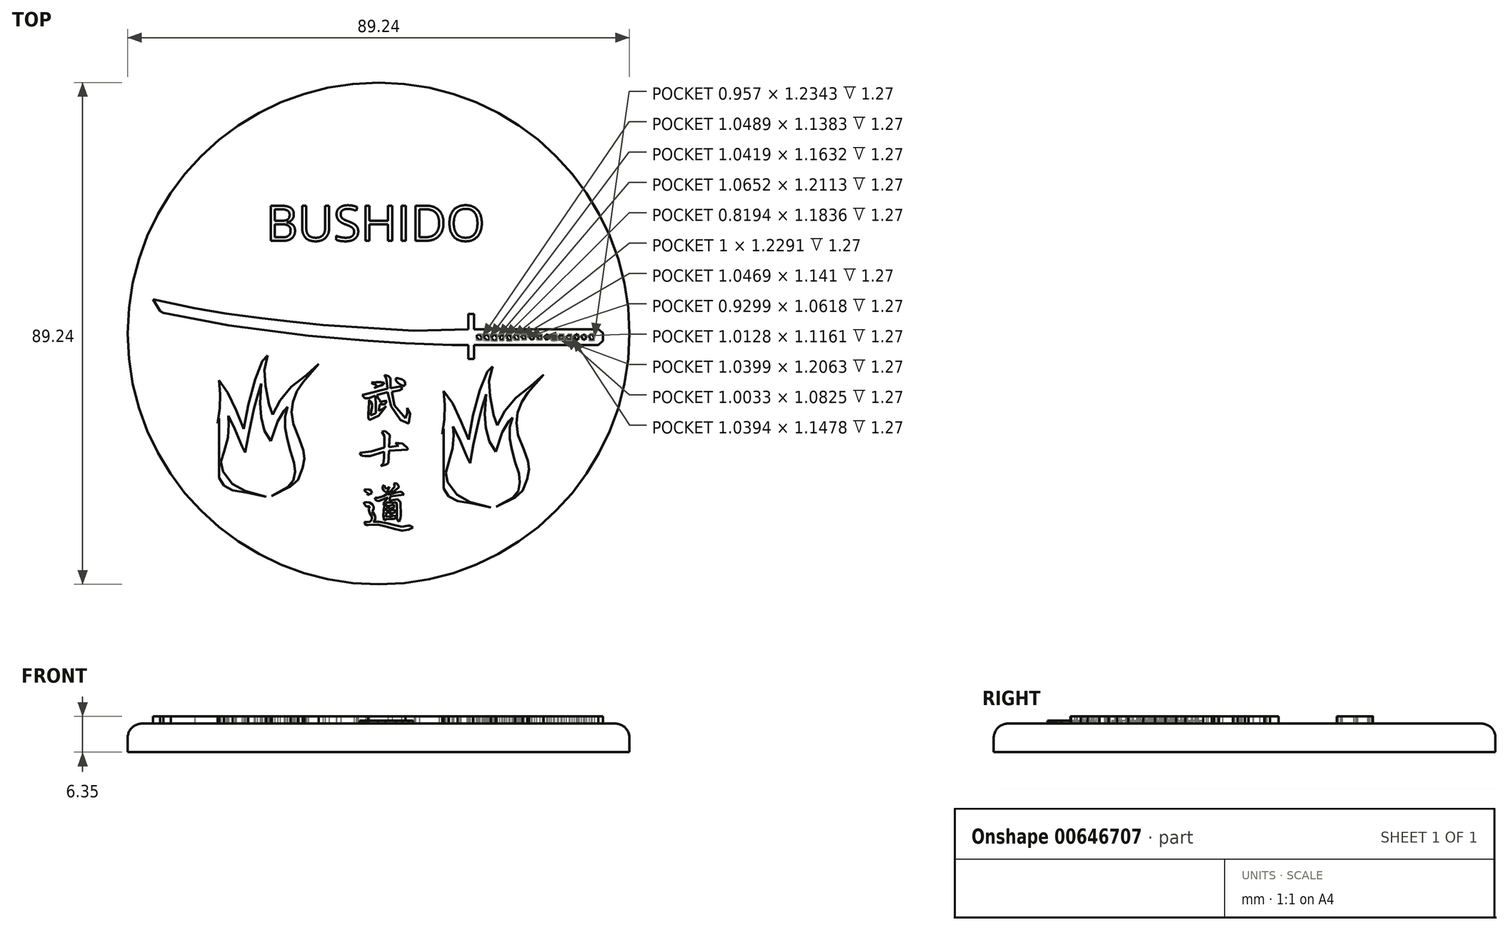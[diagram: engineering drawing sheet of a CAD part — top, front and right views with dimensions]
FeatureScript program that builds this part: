
annotation { "Feature Type Name" : "Feature", "Feature Type Description" : "" }
export const myFeature = defineFeature(function(context is Context, id is Id, definition is map)
    precondition{}
    {
        {
            var Q0;
            Q0=qCreatedBy(makeId("Top.planeOp"),FACE);
            var sketch = newSketch(context, id + "F0", { "sketchPlane" : qUnion([Q0])});
            skCircle(sketch, "E0", {"center": v(38.1, 0) * mm, "radius": 44.62 * mm});
            skSolve(sketch);
        }
        {
            var Q0;
            Q0 = qSketchRegion(id + "F0", true);
            extrude(context, id + "F1", {"entities" : qUnion([Q0]), "oppositeDirection" : true, "depth" : 5.08 * mm, "offsetDistance" : 25.4 * mm});
        }
        {
            var Q0;
            Q0=makeQuery(id+"F1.opExtrude","CAP_EDGE",EDGE,{"disambiguationData":[OSD([sQuery(id+"F0.wireOp",EDGE,"E0")])],"isStart":true});
            fillet(context, id + "F2", {"entities" : qUnion([Q0]), "radius" : 2.54 * mm, "tangentPropagation" : true, "allowEdgeOverflow" : false});
        }
        {
            var Q0;
            Q0=qCreatedBy(makeId("Top.planeOp"),FACE);
            var sketch = newSketch(context, id + "F3", { "sketchPlane" : qUnion([Q0])});
            skText(sketch, "E1", { "text": "BUSHIDO", "fontName": "OpenSans-Regular.ttf"});
            const initialGuessF3  = {"E1": [0.01806, 0.01647, 1, 0, 0.0063]};
            skSetInitialGuess(sketch, initialGuessF3);
            skSolve(sketch);
        }
        {
            var Q0;
            Q0 = qSketchRegion(id + "F3", true);
            extrude(context, id + "F4", {"entities" : qUnion([Q0]), "operationType" : NewBodyOperationType.ADD, "depth" : 1.27 * mm, "offsetDistance" : 25.4 * mm});
        }
        {
            var Q0;
            Q0=qCreatedBy(makeId("Top.planeOp"),FACE);
            var sketch = newSketch(context, id + "F5", { "sketchPlane" : qUnion([Q0])});
            skFitSpline(sketch, "E2", {"points": [v(36.87, -8.8) * mm, v(39.08, -8.86) * mm, v(37.37, -9.64) * mm, v(37.76, -9.3) * mm, v(36.87, -8.8) * mm]});
            skFitSpline(sketch, "E3", {"points": [v(41.13, -8.13) * mm, v(42.6, -9.31) * mm, v(42.62, -8.43) * mm, v(41.13, -8.13) * mm]});
            skLineSegment(sketch, "E4", {"start": v(39.12, -7.4) * mm, "end": v(39.8, -7.55) * mm});
            skLineSegment(sketch, "E5", {"start": v(39.8, -7.55) * mm, "end": v(40.25, -8) * mm});
            skLineSegment(sketch, "E6", {"start": v(40.25, -8) * mm, "end": v(40.25, -9.71) * mm});
            skLineSegment(sketch, "E7", {"start": v(40.25, -9.71) * mm, "end": v(41.91, -9.43) * mm});
            skLineSegment(sketch, "E8", {"start": v(41.91, -9.43) * mm, "end": v(42.4, -9.8) * mm});
            skLineSegment(sketch, "E9", {"start": v(42.4, -9.8) * mm, "end": v(41.8, -10.12) * mm});
            skLineSegment(sketch, "E10", {"start": v(41.8, -10.12) * mm, "end": v(40.46, -10.36) * mm});
            skLineSegment(sketch, "E11", {"start": v(40.46, -10.36) * mm, "end": v(40.91, -12.82) * mm});
            skLineSegment(sketch, "E12", {"start": v(40.91, -12.82) * mm, "end": v(42.89, -15.1) * mm});
            skLineSegment(sketch, "E13", {"start": v(42.89, -15.1) * mm, "end": v(43.22, -14.21) * mm});
            skLineSegment(sketch, "E14", {"start": v(43.22, -14.21) * mm, "end": v(43.22, -13.25) * mm});
            skLineSegment(sketch, "E15", {"start": v(43.22, -13.25) * mm, "end": v(43.7, -14.33) * mm});
            skLineSegment(sketch, "E16", {"start": v(43.7, -14.33) * mm, "end": v(43.48, -16.01) * mm});
            skLineSegment(sketch, "E17", {"start": v(43.48, -16.01) * mm, "end": v(42, -15.42) * mm});
            skLineSegment(sketch, "E18", {"start": v(42, -15.42) * mm, "end": v(40.34, -13) * mm});
            skLineSegment(sketch, "E19", {"start": v(40.34, -13) * mm, "end": v(39.71, -10.46) * mm});
            skLineSegment(sketch, "E20", {"start": v(39.71, -10.46) * mm, "end": v(37.83, -10.93) * mm});
            skLineSegment(sketch, "E21", {"start": v(37.83, -10.93) * mm, "end": v(37.97, -11.5) * mm});
            skLineSegment(sketch, "E22", {"start": v(37.97, -11.5) * mm, "end": v(38.35, -11.88) * mm});
            skLineSegment(sketch, "E23", {"start": v(38.35, -11.88) * mm, "end": v(38.35, -12.22) * mm});
            skLineSegment(sketch, "E24", {"start": v(38.35, -12.22) * mm, "end": v(39.04, -12.01) * mm});
            skLineSegment(sketch, "E25", {"start": v(39.04, -12.01) * mm, "end": v(39.58, -12.01) * mm});
            skLineSegment(sketch, "E26", {"start": v(39.58, -12.01) * mm, "end": v(39.22, -12.62) * mm});
            skLineSegment(sketch, "E27", {"start": v(39.22, -12.62) * mm, "end": v(38.32, -12.62) * mm});
            skLineSegment(sketch, "E28", {"start": v(38.32, -12.62) * mm, "end": v(38.1, -13.77) * mm});
            skLineSegment(sketch, "E29", {"start": v(38.1, -13.77) * mm, "end": v(38.89, -13.4) * mm});
            skLineSegment(sketch, "E30", {"start": v(38.89, -13.4) * mm, "end": v(39.48, -12.91) * mm});
            skLineSegment(sketch, "E31", {"start": v(39.48, -12.91) * mm, "end": v(38.1, -14.61) * mm});
            skLineSegment(sketch, "E32", {"start": v(38.1, -14.61) * mm, "end": v(36.46, -15.42) * mm});
            skLineSegment(sketch, "E33", {"start": v(36.46, -15.42) * mm, "end": v(36.25, -15) * mm});
            skLineSegment(sketch, "E34", {"start": v(36.25, -15) * mm, "end": v(36.25, -14.29) * mm});
            skLineSegment(sketch, "E35", {"start": v(36.25, -14.29) * mm, "end": v(36.42, -12.37) * mm});
            skLineSegment(sketch, "E36", {"start": v(36.42, -12.37) * mm, "end": v(36.42, -11.82) * mm});
            skLineSegment(sketch, "E37", {"start": v(36.42, -11.82) * mm, "end": v(36.82, -12.28) * mm});
            skLineSegment(sketch, "E38", {"start": v(36.82, -12.28) * mm, "end": v(36.96, -12.83) * mm});
            skLineSegment(sketch, "E39", {"start": v(36.96, -12.83) * mm, "end": v(36.65, -14.56) * mm});
            skLineSegment(sketch, "E40", {"start": v(36.65, -14.56) * mm, "end": v(37.65, -14.17) * mm});
            skLineSegment(sketch, "E41", {"start": v(37.65, -14.17) * mm, "end": v(37.65, -12.26) * mm});
            skLineSegment(sketch, "E42", {"start": v(37.65, -12.26) * mm, "end": v(37.47, -11.07) * mm});
            skLineSegment(sketch, "E43", {"start": v(37.47, -11.07) * mm, "end": v(36.42, -11.5) * mm});
            skLineSegment(sketch, "E44", {"start": v(36.42, -11.5) * mm, "end": v(35.66, -11.5) * mm});
            skLineSegment(sketch, "E45", {"start": v(35.66, -11.5) * mm, "end": v(35.18, -10.96) * mm});
            skLineSegment(sketch, "E46", {"start": v(35.18, -10.96) * mm, "end": v(35.94, -10.79) * mm});
            skLineSegment(sketch, "E47", {"start": v(35.94, -10.79) * mm, "end": v(39.7, -9.8) * mm});
            skLineSegment(sketch, "E48", {"start": v(39.7, -9.8) * mm, "end": v(39.48, -7.93) * mm});
            skLineSegment(sketch, "E49", {"start": v(39.48, -7.93) * mm, "end": v(39.12, -7.4) * mm});
            skLineSegment(sketch, "E50", {"start": v(38.67, -17.5) * mm, "end": v(39.12, -17.36) * mm});
            skLineSegment(sketch, "E51", {"start": v(39.12, -17.36) * mm, "end": v(39.48, -17.5) * mm});
            skLineSegment(sketch, "E52", {"start": v(39.48, -17.5) * mm, "end": v(40.1, -18.05) * mm});
            skLineSegment(sketch, "E53", {"start": v(40.1, -18.05) * mm, "end": v(39.95, -20.19) * mm});
            skLineSegment(sketch, "E54", {"start": v(39.95, -20.19) * mm, "end": v(41.68, -19.95) * mm});
            skLineSegment(sketch, "E55", {"start": v(41.68, -19.95) * mm, "end": v(41.48, -19.87) * mm});
            skLineSegment(sketch, "E56", {"start": v(41.48, -19.87) * mm, "end": v(41.13, -19.45) * mm});
            skLineSegment(sketch, "E57", {"start": v(41.13, -19.45) * mm, "end": v(42.35, -19.6) * mm});
            skLineSegment(sketch, "E58", {"start": v(42.35, -19.6) * mm, "end": v(43.27, -20.43) * mm});
            skLineSegment(sketch, "E59", {"start": v(43.27, -20.43) * mm, "end": v(43.27, -20.67) * mm});
            skLineSegment(sketch, "E60", {"start": v(43.27, -20.67) * mm, "end": v(39.97, -20.88) * mm});
            skLineSegment(sketch, "E61", {"start": v(39.97, -20.88) * mm, "end": v(39.8, -23.09) * mm});
            skLineSegment(sketch, "E62", {"start": v(39.8, -23.09) * mm, "end": v(39.4, -23.33) * mm});
            skLineSegment(sketch, "E63", {"start": v(39.4, -23.33) * mm, "end": v(38.52, -23.59) * mm});
            skLineSegment(sketch, "E64", {"start": v(38.52, -23.59) * mm, "end": v(38.97, -23.12) * mm});
            skLineSegment(sketch, "E65", {"start": v(38.97, -23.12) * mm, "end": v(39.1, -22.1) * mm});
            skLineSegment(sketch, "E66", {"start": v(39.1, -22.1) * mm, "end": v(39.1, -21.04) * mm});
            skLineSegment(sketch, "E67", {"start": v(39.1, -21.04) * mm, "end": v(36.57, -21.83) * mm});
            skLineSegment(sketch, "E68", {"start": v(36.57, -21.83) * mm, "end": v(35.67, -21.83) * mm});
            skLineSegment(sketch, "E69", {"start": v(35.67, -21.83) * mm, "end": v(35.05, -21.75) * mm});
            skLineSegment(sketch, "E70", {"start": v(35.05, -21.75) * mm, "end": v(34.79, -21.22) * mm});
            skLineSegment(sketch, "E71", {"start": v(34.79, -21.22) * mm, "end": v(36.77, -21.01) * mm});
            skLineSegment(sketch, "E72", {"start": v(36.77, -21.01) * mm, "end": v(39.12, -20.3) * mm});
            skLineSegment(sketch, "E73", {"start": v(39.12, -20.3) * mm, "end": v(39.12, -18.27) * mm});
            skLineSegment(sketch, "E74", {"start": v(39.12, -18.27) * mm, "end": v(38.67, -17.5) * mm});
            skLineSegment(sketch, "E75", {"start": v(36.68, -23.95) * mm, "end": v(39.03, -23.68) * mm});
            skLineSegment(sketch, "E76", {"start": v(39.03, -23.68) * mm, "end": v(40.38, -23.47) * mm});
            skLineSegment(sketch, "E77", {"start": v(40.38, -23.47) * mm, "end": v(40.97, -23.31) * mm});
            skLineSegment(sketch, "E78", {"start": v(40.97, -23.31) * mm, "end": v(41.37, -23.33) * mm});
            skLineSegment(sketch, "E79", {"start": v(41.37, -23.33) * mm, "end": v(41.87, -23.54) * mm});
            skLineSegment(sketch, "E80", {"start": v(41.87, -23.54) * mm, "end": v(42.09, -24.07) * mm});
            skLineSegment(sketch, "E81", {"start": v(42.09, -24.07) * mm, "end": v(41.49, -24.07) * mm});
            skLineSegment(sketch, "E82", {"start": v(41.49, -24.07) * mm, "end": v(40.58, -24.07) * mm});
            skLineSegment(sketch, "E83", {"start": v(40.58, -24.07) * mm, "end": v(39.63, -24.07) * mm});
            skLineSegment(sketch, "E84", {"start": v(39.63, -24.07) * mm, "end": v(38.25, -24.4) * mm});
            skLineSegment(sketch, "E85", {"start": v(38.25, -24.4) * mm, "end": v(37.39, -24.54) * mm});
            skLineSegment(sketch, "E86", {"start": v(37.39, -24.54) * mm, "end": v(37.06, -24.4) * mm});
            skLineSegment(sketch, "E87", {"start": v(37.06, -24.4) * mm, "end": v(36.67, -23.98) * mm});
            skLineSegment(sketch, "E88", {"start": v(35.58, -27.68) * mm, "end": v(36.47, -27.8) * mm});
            skLineSegment(sketch, "E89", {"start": v(36.47, -27.8) * mm, "end": v(36.8, -27.96) * mm});
            skLineSegment(sketch, "E90", {"start": v(36.8, -27.96) * mm, "end": v(36.91, -28.4) * mm});
            skLineSegment(sketch, "E91", {"start": v(36.91, -28.4) * mm, "end": v(36.14, -28.72) * mm});
            skLineSegment(sketch, "E92", {"start": v(36.14, -28.72) * mm, "end": v(36.11, -28.5) * mm});
            skLineSegment(sketch, "E93", {"start": v(36.11, -28.5) * mm, "end": v(36.3, -28.47) * mm});
            skLineSegment(sketch, "E94", {"start": v(36.3, -28.47) * mm, "end": v(35.68, -28.12) * mm});
            skLineSegment(sketch, "E95", {"start": v(35.68, -28.12) * mm, "end": v(35.58, -27.68) * mm});
            skLineSegment(sketch, "E96", {"start": v(39.12, -26.98) * mm, "end": v(39.18, -27.25) * mm});
            skLineSegment(sketch, "E97", {"start": v(39.18, -27.25) * mm, "end": v(39.48, -27.62) * mm});
            skLineSegment(sketch, "E98", {"start": v(39.48, -27.62) * mm, "end": v(40.02, -27.28) * mm});
            skLineSegment(sketch, "E99", {"start": v(40.02, -27.28) * mm, "end": v(39.59, -28.37) * mm});
            skLineSegment(sketch, "E100", {"start": v(39.59, -28.37) * mm, "end": v(39.03, -28) * mm});
            skLineSegment(sketch, "E101", {"start": v(39.03, -28) * mm, "end": v(38.8, -27.55) * mm});
            skLineSegment(sketch, "E102", {"start": v(38.8, -27.55) * mm, "end": v(38.8, -27.17) * mm});
            skLineSegment(sketch, "E103", {"start": v(38.8, -27.17) * mm, "end": v(39.12, -26.98) * mm});
            skLineSegment(sketch, "E104", {"start": v(40.91, -26.65) * mm, "end": v(41.37, -26.7) * mm});
            skLineSegment(sketch, "E105", {"start": v(41.37, -26.7) * mm, "end": v(41.65, -27.13) * mm});
            skLineSegment(sketch, "E106", {"start": v(41.65, -27.13) * mm, "end": v(41.7, -27.39) * mm});
            skLineSegment(sketch, "E107", {"start": v(41.7, -27.39) * mm, "end": v(40.66, -28.2) * mm});
            skLineSegment(sketch, "E108", {"start": v(40.66, -28.2) * mm, "end": v(39.79, -28.58) * mm});
            skLineSegment(sketch, "E109", {"start": v(39.79, -28.58) * mm, "end": v(40.16, -28.63) * mm});
            skLineSegment(sketch, "E110", {"start": v(40.16, -28.63) * mm, "end": v(41.23, -28.26) * mm});
            skLineSegment(sketch, "E111", {"start": v(41.23, -28.26) * mm, "end": v(42.02, -28.17) * mm});
            skLineSegment(sketch, "E112", {"start": v(42.02, -28.17) * mm, "end": v(42.31, -28.29) * mm});
            skLineSegment(sketch, "E113", {"start": v(42.31, -28.29) * mm, "end": v(42.66, -28.63) * mm});
            skLineSegment(sketch, "E114", {"start": v(42.66, -28.63) * mm, "end": v(40.16, -28.98) * mm});
            skLineSegment(sketch, "E115", {"start": v(40.16, -28.98) * mm, "end": v(40.1, -29.66) * mm});
            skLineSegment(sketch, "E116", {"start": v(40.1, -29.66) * mm, "end": v(40, -29.8) * mm});
            skLineSegment(sketch, "E117", {"start": v(40, -29.8) * mm, "end": v(40.71, -29.6) * mm});
            skLineSegment(sketch, "E118", {"start": v(40.71, -29.6) * mm, "end": v(41.52, -29.48) * mm});
            skLineSegment(sketch, "E119", {"start": v(41.52, -29.48) * mm, "end": v(41.97, -29.97) * mm});
            skLineSegment(sketch, "E120", {"start": v(41.97, -29.97) * mm, "end": v(42.05, -32.42) * mm});
            skLineSegment(sketch, "E121", {"start": v(42.05, -32.42) * mm, "end": v(42, -32.78) * mm});
            skLineSegment(sketch, "E122", {"start": v(42, -32.78) * mm, "end": v(41.72, -33.48) * mm});
            skLineSegment(sketch, "E123", {"start": v(41.72, -33.48) * mm, "end": v(41.37, -33.06) * mm});
            skLineSegment(sketch, "E124", {"start": v(41.37, -33.06) * mm, "end": v(41.37, -31) * mm});
            skLineSegment(sketch, "E125", {"start": v(41.37, -31) * mm, "end": v(41.37, -30.48) * mm});
            skLineSegment(sketch, "E126", {"start": v(41.37, -30.48) * mm, "end": v(41.2, -30.01) * mm});
            skLineSegment(sketch, "E127", {"start": v(41.2, -30.01) * mm, "end": v(40.72, -30.12) * mm});
            skLineSegment(sketch, "E128", {"start": v(40.72, -30.12) * mm, "end": v(40.07, -30.04) * mm});
            skLineSegment(sketch, "E129", {"start": v(40.07, -30.04) * mm, "end": v(39.65, -30.04) * mm});
            skLineSegment(sketch, "E130", {"start": v(39.65, -30.04) * mm, "end": v(39.38, -30.22) * mm});
            skLineSegment(sketch, "E131", {"start": v(39.38, -30.22) * mm, "end": v(39.48, -30.6) * mm});
            skLineSegment(sketch, "E132", {"start": v(39.48, -30.6) * mm, "end": v(39.52, -30.7) * mm});
            skLineSegment(sketch, "E133", {"start": v(39.52, -30.7) * mm, "end": v(40.08, -30.62) * mm});
            skLineSegment(sketch, "E134", {"start": v(40.08, -30.62) * mm, "end": v(40.54, -30.5) * mm});
            skLineSegment(sketch, "E135", {"start": v(40.54, -30.5) * mm, "end": v(40.82, -30.53) * mm});
            skLineSegment(sketch, "E136", {"start": v(40.82, -30.53) * mm, "end": v(41, -30.7) * mm});
            skLineSegment(sketch, "E137", {"start": v(41, -30.7) * mm, "end": v(40.77, -30.92) * mm});
            skLineSegment(sketch, "E138", {"start": v(40.77, -30.92) * mm, "end": v(40.23, -31.11) * mm});
            skLineSegment(sketch, "E139", {"start": v(40.23, -31.11) * mm, "end": v(39.96, -31.3) * mm});
            skLineSegment(sketch, "E140", {"start": v(39.96, -31.3) * mm, "end": v(39.89, -31.25) * mm});
            skLineSegment(sketch, "E141", {"start": v(39.89, -31.25) * mm, "end": v(40.08, -31.1) * mm});
            skLineSegment(sketch, "E142", {"start": v(40.08, -31.1) * mm, "end": v(39.97, -31.05) * mm});
            skLineSegment(sketch, "E143", {"start": v(39.97, -31.05) * mm, "end": v(39.45, -31.04) * mm});
            skLineSegment(sketch, "E144", {"start": v(39.45, -31.04) * mm, "end": v(39.45, -31.55) * mm});
            skLineSegment(sketch, "E145", {"start": v(39.45, -31.55) * mm, "end": v(39.88, -31.55) * mm});
            skLineSegment(sketch, "E146", {"start": v(39.88, -31.55) * mm, "end": v(40.56, -31.39) * mm});
            skLineSegment(sketch, "E147", {"start": v(40.56, -31.39) * mm, "end": v(40.92, -31.39) * mm});
            skLineSegment(sketch, "E148", {"start": v(40.92, -31.39) * mm, "end": v(41.1, -31.54) * mm});
            skLineSegment(sketch, "E149", {"start": v(41.1, -31.54) * mm, "end": v(41.01, -31.77) * mm});
            skLineSegment(sketch, "E150", {"start": v(41.01, -31.77) * mm, "end": v(40.5, -32) * mm});
            skLineSegment(sketch, "E151", {"start": v(40.5, -32) * mm, "end": v(40.14, -32.26) * mm});
            skLineSegment(sketch, "E152", {"start": v(40.14, -32.26) * mm, "end": v(40.1, -32.2) * mm});
            skLineSegment(sketch, "E153", {"start": v(40.1, -32.2) * mm, "end": v(40.4, -31.9) * mm});
            skLineSegment(sketch, "E154", {"start": v(40.4, -31.9) * mm, "end": v(39.5, -31.82) * mm});
            skLineSegment(sketch, "E155", {"start": v(39.5, -31.82) * mm, "end": v(39.43, -32) * mm});
            skLineSegment(sketch, "E156", {"start": v(39.43, -32) * mm, "end": v(39.4, -32.6) * mm});
            skLineSegment(sketch, "E157", {"start": v(39.4, -32.6) * mm, "end": v(39.68, -32.47) * mm});
            skLineSegment(sketch, "E158", {"start": v(39.68, -32.47) * mm, "end": v(39.66, -32.54) * mm});
            skLineSegment(sketch, "E159", {"start": v(39.66, -32.54) * mm, "end": v(40.06, -32.58) * mm});
            skLineSegment(sketch, "E160", {"start": v(40.06, -32.58) * mm, "end": v(40.73, -32.43) * mm});
            skLineSegment(sketch, "E161", {"start": v(40.73, -32.43) * mm, "end": v(41.09, -32.5) * mm});
            skLineSegment(sketch, "E162", {"start": v(41.09, -32.5) * mm, "end": v(41.24, -32.77) * mm});
            skLineSegment(sketch, "E163", {"start": v(41.24, -32.77) * mm, "end": v(41.2, -32.87) * mm});
            skLineSegment(sketch, "E164", {"start": v(41.2, -32.87) * mm, "end": v(40.82, -32.96) * mm});
            skLineSegment(sketch, "E165", {"start": v(40.82, -32.96) * mm, "end": v(40.08, -32.96) * mm});
            skLineSegment(sketch, "E166", {"start": v(40.08, -32.96) * mm, "end": v(39.52, -33.03) * mm});
            skLineSegment(sketch, "E167", {"start": v(39.52, -33.03) * mm, "end": v(39.17, -33.23) * mm});
            skLineSegment(sketch, "E168", {"start": v(39.17, -33.23) * mm, "end": v(38.92, -32.52) * mm});
            skLineSegment(sketch, "E169", {"start": v(38.92, -32.52) * mm, "end": v(39.01, -31.43) * mm});
            skLineSegment(sketch, "E170", {"start": v(39.01, -31.43) * mm, "end": v(39.1, -30.66) * mm});
            skLineSegment(sketch, "E171", {"start": v(39.1, -30.66) * mm, "end": v(38.97, -30.25) * mm});
            skLineSegment(sketch, "E172", {"start": v(38.97, -30.25) * mm, "end": v(39.77, -29.15) * mm});
            skLineSegment(sketch, "E173", {"start": v(39.77, -29.15) * mm, "end": v(38.12, -29.79) * mm});
            skLineSegment(sketch, "E174", {"start": v(38.12, -29.79) * mm, "end": v(37.73, -29.75) * mm});
            skLineSegment(sketch, "E175", {"start": v(37.73, -29.75) * mm, "end": v(37.5, -29.5) * mm});
            skLineSegment(sketch, "E176", {"start": v(37.5, -29.5) * mm, "end": v(37.46, -29.23) * mm});
            skLineSegment(sketch, "E177", {"start": v(37.46, -29.23) * mm, "end": v(38.03, -29.23) * mm});
            skLineSegment(sketch, "E178", {"start": v(38.03, -29.23) * mm, "end": v(39.04, -28.91) * mm});
            skLineSegment(sketch, "E179", {"start": v(39.04, -28.91) * mm, "end": v(40.1, -28.19) * mm});
            skLineSegment(sketch, "E180", {"start": v(40.1, -28.19) * mm, "end": v(40.98, -27.24) * mm});
            skLineSegment(sketch, "E181", {"start": v(40.98, -27.24) * mm, "end": v(40.9, -26.92) * mm});
            skLineSegment(sketch, "E182", {"start": v(40.9, -26.92) * mm, "end": v(40.85, -26.71) * mm});
            skLineSegment(sketch, "E183", {"start": v(40.85, -26.71) * mm, "end": v(40.92, -26.63) * mm});
            skLineSegment(sketch, "E184", {"start": v(40.92, -26.63) * mm, "end": v(40.91, -26.65) * mm});
            skLineSegment(sketch, "E185", {"start": v(35.52, -30.07) * mm, "end": v(35.98, -30.02) * mm});
            skLineSegment(sketch, "E186", {"start": v(35.98, -30.02) * mm, "end": v(36.47, -30.08) * mm});
            skLineSegment(sketch, "E187", {"start": v(36.47, -30.08) * mm, "end": v(37, -30.38) * mm});
            skLineSegment(sketch, "E188", {"start": v(37, -30.38) * mm, "end": v(37.22, -30.76) * mm});
            skLineSegment(sketch, "E189", {"start": v(37.22, -30.76) * mm, "end": v(37.22, -31.2) * mm});
            skLineSegment(sketch, "E190", {"start": v(37.22, -31.2) * mm, "end": v(36.95, -31.62) * mm});
            skLineSegment(sketch, "E191", {"start": v(36.95, -31.62) * mm, "end": v(37.42, -32.38) * mm});
            skLineSegment(sketch, "E192", {"start": v(37.42, -32.38) * mm, "end": v(37.53, -32.82) * mm});
            skLineSegment(sketch, "E193", {"start": v(37.53, -32.82) * mm, "end": v(37.43, -33.26) * mm});
            skLineSegment(sketch, "E194", {"start": v(37.43, -33.26) * mm, "end": v(37.14, -33.5) * mm});
            skLineSegment(sketch, "E195", {"start": v(37.14, -33.5) * mm, "end": v(38.1, -33.5) * mm});
            skLineSegment(sketch, "E196", {"start": v(38.1, -33.5) * mm, "end": v(39.56, -33.74) * mm});
            skLineSegment(sketch, "E197", {"start": v(39.56, -33.74) * mm, "end": v(41.1, -34.14) * mm});
            skLineSegment(sketch, "E198", {"start": v(41.1, -34.14) * mm, "end": v(42.26, -34.37) * mm});
            skLineSegment(sketch, "E199", {"start": v(42.26, -34.37) * mm, "end": v(43.32, -34.19) * mm});
            skLineSegment(sketch, "E200", {"start": v(43.32, -34.19) * mm, "end": v(43.79, -34.19) * mm});
            skLineSegment(sketch, "E201", {"start": v(43.79, -34.19) * mm, "end": v(44.23, -34.52) * mm});
            skLineSegment(sketch, "E202", {"start": v(44.23, -34.52) * mm, "end": v(43.48, -34.92) * mm});
            skLineSegment(sketch, "E203", {"start": v(43.48, -34.92) * mm, "end": v(42.28, -35.06) * mm});
            skLineSegment(sketch, "E204", {"start": v(42.28, -35.06) * mm, "end": v(41.16, -34.8) * mm});
            skLineSegment(sketch, "E205", {"start": v(41.16, -34.8) * mm, "end": v(39.3, -34.3) * mm});
            skLineSegment(sketch, "E206", {"start": v(39.3, -34.3) * mm, "end": v(37.97, -34.02) * mm});
            skLineSegment(sketch, "E207", {"start": v(37.97, -34.02) * mm, "end": v(36.27, -34.06) * mm});
            skLineSegment(sketch, "E208", {"start": v(36.27, -34.06) * mm, "end": v(35.94, -34.06) * mm});
            skLineSegment(sketch, "E209", {"start": v(35.94, -34.06) * mm, "end": v(35.64, -33.85) * mm});
            skLineSegment(sketch, "E210", {"start": v(35.64, -33.85) * mm, "end": v(35.64, -33.5) * mm});
            skLineSegment(sketch, "E211", {"start": v(35.64, -33.5) * mm, "end": v(36.1, -33.55) * mm});
            skLineSegment(sketch, "E212", {"start": v(36.1, -33.55) * mm, "end": v(36.6, -33.46) * mm});
            skLineSegment(sketch, "E213", {"start": v(36.6, -33.46) * mm, "end": v(36.95, -33.01) * mm});
            skLineSegment(sketch, "E214", {"start": v(36.95, -33.01) * mm, "end": v(36.95, -32.53) * mm});
            skLineSegment(sketch, "E215", {"start": v(36.95, -32.53) * mm, "end": v(36.46, -31.83) * mm});
            skLineSegment(sketch, "E216", {"start": v(36.46, -31.83) * mm, "end": v(36.35, -31.22) * mm});
            skLineSegment(sketch, "E217", {"start": v(36.35, -31.22) * mm, "end": v(36.54, -30.77) * mm});
            skLineSegment(sketch, "E218", {"start": v(36.54, -30.77) * mm, "end": v(36.3, -30.74) * mm});
            skLineSegment(sketch, "E219", {"start": v(36.3, -30.74) * mm, "end": v(35.93, -30.74) * mm});
            skLineSegment(sketch, "E220", {"start": v(35.93, -30.74) * mm, "end": v(35.63, -30.47) * mm});
            skLineSegment(sketch, "E221", {"start": v(35.63, -30.47) * mm, "end": v(35.52, -30.2) * mm});
            skLineSegment(sketch, "E222", {"start": v(35.52, -30.2) * mm, "end": v(35.52, -30.07) * mm});
            skSolve(sketch);
        }
        {
            var Q0;
            Q0 = qSketchRegion(id + "F5", true);
            extrude(context, id + "F6", {"entities" : qUnion([Q0]), "operationType" : NewBodyOperationType.ADD, "depth" : 0.5 * mm, "offsetDistance" : 25.4 * mm});
        }
        {
            var Q0;
            Q0=qCreatedBy(makeId("Top.planeOp"),FACE);
            var sketch = newSketch(context, id + "F7", { "sketchPlane" : qUnion([Q0])});
            skLineSegment(sketch, "E223", {"start": v(-64.44, 4.36) * mm, "end": v(-42.37, 4.36) * mm});
            skLineSegment(sketch, "E224", {"start": v(-42.37, 4.36) * mm, "end": v(-41.55, 3.73) * mm});
            skLineSegment(sketch, "E225", {"start": v(-41.55, 3.73) * mm, "end": v(-41.55, 2.36) * mm});
            skLineSegment(sketch, "E226", {"start": v(-41.55, 2.36) * mm, "end": v(-42.37, 1.59) * mm});
            skLineSegment(sketch, "E227", {"start": v(-42.37, 1.59) * mm, "end": v(-64.44, 1.59) * mm});
            skLineSegment(sketch, "E228", {"start": v(-65.5, 7.14) * mm, "end": v(-64.44, 7.14) * mm});
            skLineSegment(sketch, "E229", {"start": v(-64.44, 7.14) * mm, "end": v(-64.44, -0.92) * mm});
            skLineSegment(sketch, "E230", {"start": v(-64.44, -0.92) * mm, "end": v(-65.5, -0.88) * mm});
            skLineSegment(sketch, "E231", {"start": v(-65.5, -0.88) * mm, "end": v(-65.5, 7.14) * mm});
            skLineSegment(sketch, "E232", {"start": v(-63.55, 3.52) * mm, "end": v(-64.08, 3.1) * mm});
            skLineSegment(sketch, "E233", {"start": v(-64.08, 3.1) * mm, "end": v(-63.5, 2.39) * mm});
            skLineSegment(sketch, "E234", {"start": v(-63.5, 2.39) * mm, "end": v(-63.03, 2.77) * mm});
            skLineSegment(sketch, "E235", {"start": v(-63.03, 2.77) * mm, "end": v(-63.55, 3.52) * mm});
            skLineSegment(sketch, "E236", {"start": v(-62.23, 3.52) * mm, "end": v(-62.73, 2.95) * mm});
            skLineSegment(sketch, "E237", {"start": v(-62.73, 2.95) * mm, "end": v(-62.06, 2.36) * mm});
            skLineSegment(sketch, "E238", {"start": v(-62.06, 2.36) * mm, "end": v(-61.7, 2.78) * mm});
            skLineSegment(sketch, "E239", {"start": v(-61.7, 2.78) * mm, "end": v(-62.23, 3.52) * mm});
            skLineSegment(sketch, "E240", {"start": v(-60.84, 3.52) * mm, "end": v(-61.39, 2.82) * mm});
            skLineSegment(sketch, "E241", {"start": v(-61.39, 2.82) * mm, "end": v(-60.74, 2.31) * mm});
            skLineSegment(sketch, "E242", {"start": v(-60.74, 2.31) * mm, "end": v(-60.32, 2.84) * mm});
            skLineSegment(sketch, "E243", {"start": v(-60.32, 2.84) * mm, "end": v(-60.84, 3.52) * mm});
            skLineSegment(sketch, "E244", {"start": v(-59.55, 3.52) * mm, "end": v(-59.98, 2.9) * mm});
            skLineSegment(sketch, "E245", {"start": v(-59.98, 2.9) * mm, "end": v(-59.6, 2.34) * mm});
            skLineSegment(sketch, "E246", {"start": v(-59.6, 2.34) * mm, "end": v(-59.16, 2.89) * mm});
            skLineSegment(sketch, "E247", {"start": v(-59.16, 2.89) * mm, "end": v(-59.55, 3.52) * mm});
            skLineSegment(sketch, "E248", {"start": v(-58.23, 3.52) * mm, "end": v(-58.7, 3) * mm});
            skLineSegment(sketch, "E249", {"start": v(-58.7, 3) * mm, "end": v(-58.25, 2.3) * mm});
            skLineSegment(sketch, "E250", {"start": v(-58.25, 2.3) * mm, "end": v(-57.7, 2.65) * mm});
            skLineSegment(sketch, "E251", {"start": v(-57.7, 2.65) * mm, "end": v(-58.23, 3.52) * mm});
            skLineSegment(sketch, "E252", {"start": v(-56.9, 3.52) * mm, "end": v(-57.43, 3.02) * mm});
            skLineSegment(sketch, "E253", {"start": v(-57.43, 3.02) * mm, "end": v(-56.82, 2.38) * mm});
            skLineSegment(sketch, "E254", {"start": v(-56.82, 2.38) * mm, "end": v(-56.38, 2.77) * mm});
            skLineSegment(sketch, "E255", {"start": v(-56.38, 2.77) * mm, "end": v(-56.9, 3.52) * mm});
            skLineSegment(sketch, "E256", {"start": v(-55.59, 3.52) * mm, "end": v(-56.09, 3.1) * mm});
            skLineSegment(sketch, "E257", {"start": v(-56.09, 3.1) * mm, "end": v(-55.54, 2.46) * mm});
            skLineSegment(sketch, "E258", {"start": v(-55.54, 2.46) * mm, "end": v(-55.16, 2.8) * mm});
            skLineSegment(sketch, "E259", {"start": v(-55.16, 2.8) * mm, "end": v(-55.59, 3.52) * mm});
            skLineSegment(sketch, "E260", {"start": v(-54.17, 3.52) * mm, "end": v(-54.7, 3) * mm});
            skLineSegment(sketch, "E261", {"start": v(-54.7, 3) * mm, "end": v(-54.16, 2.47) * mm});
            skLineSegment(sketch, "E262", {"start": v(-54.16, 2.47) * mm, "end": v(-53.76, 2.8) * mm});
            skLineSegment(sketch, "E263", {"start": v(-53.76, 2.8) * mm, "end": v(-54.17, 3.52) * mm});
            skLineSegment(sketch, "E264", {"start": v(-52.79, 3.57) * mm, "end": v(-53.33, 3.1) * mm});
            skLineSegment(sketch, "E265", {"start": v(-53.33, 3.1) * mm, "end": v(-52.77, 2.45) * mm});
            skLineSegment(sketch, "E266", {"start": v(-52.77, 2.45) * mm, "end": v(-52.32, 2.85) * mm});
            skLineSegment(sketch, "E267", {"start": v(-52.32, 2.85) * mm, "end": v(-52.79, 3.57) * mm});
            skLineSegment(sketch, "E268", {"start": v(-51.37, 3.52) * mm, "end": v(-51.99, 3.07) * mm});
            skLineSegment(sketch, "E269", {"start": v(-51.99, 3.07) * mm, "end": v(-51.56, 2.5) * mm});
            skLineSegment(sketch, "E270", {"start": v(-51.56, 2.5) * mm, "end": v(-51.07, 2.86) * mm});
            skLineSegment(sketch, "E271", {"start": v(-51.07, 2.86) * mm, "end": v(-51.37, 3.52) * mm});
            skLineSegment(sketch, "E272", {"start": v(-50.15, 3.52) * mm, "end": v(-50.74, 3) * mm});
            skLineSegment(sketch, "E273", {"start": v(-50.74, 3) * mm, "end": v(-50.37, 2.32) * mm});
            skLineSegment(sketch, "E274", {"start": v(-50.37, 2.32) * mm, "end": v(-49.7, 2.68) * mm});
            skLineSegment(sketch, "E275", {"start": v(-49.7, 2.68) * mm, "end": v(-50.15, 3.52) * mm});
            skLineSegment(sketch, "E276", {"start": v(-48.85, 3.52) * mm, "end": v(-49.49, 3.05) * mm});
            skLineSegment(sketch, "E277", {"start": v(-49.49, 3.05) * mm, "end": v(-49.03, 2.44) * mm});
            skLineSegment(sketch, "E278", {"start": v(-49.03, 2.44) * mm, "end": v(-48.48, 2.85) * mm});
            skLineSegment(sketch, "E279", {"start": v(-48.48, 2.85) * mm, "end": v(-48.85, 3.52) * mm});
            skLineSegment(sketch, "E280", {"start": v(-47.46, 3.52) * mm, "end": v(-48.07, 3) * mm});
            skLineSegment(sketch, "E281", {"start": v(-48.07, 3) * mm, "end": v(-47.54, 2.38) * mm});
            skLineSegment(sketch, "E282", {"start": v(-47.54, 2.38) * mm, "end": v(-47.04, 2.8) * mm});
            skLineSegment(sketch, "E283", {"start": v(-47.04, 2.8) * mm, "end": v(-47.46, 3.52) * mm});
            skLineSegment(sketch, "E284", {"start": v(-46.07, 3.52) * mm, "end": v(-46.7, 3.16) * mm});
            skLineSegment(sketch, "E285", {"start": v(-46.7, 3.16) * mm, "end": v(-46.32, 2.48) * mm});
            skLineSegment(sketch, "E286", {"start": v(-46.32, 2.48) * mm, "end": v(-45.78, 2.78) * mm});
            skLineSegment(sketch, "E287", {"start": v(-45.78, 2.78) * mm, "end": v(-46.07, 3.52) * mm});
            skLineSegment(sketch, "E288", {"start": v(-44.8, 3.51) * mm, "end": v(-45.43, 3.16) * mm});
            skLineSegment(sketch, "E289", {"start": v(-45.43, 3.16) * mm, "end": v(-45.05, 2.46) * mm});
            skLineSegment(sketch, "E290", {"start": v(-45.05, 2.46) * mm, "end": v(-44.47, 2.78) * mm});
            skLineSegment(sketch, "E291", {"start": v(-44.47, 2.78) * mm, "end": v(-44.8, 3.51) * mm});
            skPoint(sketch, "E292.orphan", {"position": v(-44.77, 3.52) * mm});
            skLineSegment(sketch, "E293", {"start": v(-43.5, 3.59) * mm, "end": v(-44.02, 3.15) * mm});
            skPoint(sketch, "E293.endSnap0", {"position": v(-45.93, 3.15) * mm});
            skLineSegment(sketch, "E294", {"start": v(-44.02, 3.15) * mm, "end": v(-43.67, 2.36) * mm});
            skLineSegment(sketch, "E295", {"start": v(-43.67, 2.36) * mm, "end": v(-43.06, 2.86) * mm});
            skLineSegment(sketch, "E296", {"start": v(-43.06, 2.86) * mm, "end": v(-43.5, 3.59) * mm});
            skLineSegment(sketch, "E297", {"start": v(-65.5, 4.36) * mm, "end": v(-67.4, 3.28) * mm});
            skLineSegment(sketch, "E298", {"start": v(-67.4, 3.28) * mm, "end": v(-65.5, 1.59) * mm});
            skLineSegment(sketch, "E299", {"start": v(-65.5, 1.59) * mm, "end": v(-68.42, 1.59) * mm});
            skLineSegment(sketch, "E300", {"start": v(-68.42, 1.59) * mm, "end": v(-76.68, 1.9) * mm});
            skLineSegment(sketch, "E301", {"start": v(-76.68, 1.9) * mm, "end": v(-83.34, 2.32) * mm});
            skLineSegment(sketch, "E302", {"start": v(-83.34, 2.32) * mm, "end": v(-93.93, 3.22) * mm});
            skLineSegment(sketch, "E303", {"start": v(-93.93, 3.22) * mm, "end": v(-108.07, 5.1) * mm});
            skLineSegment(sketch, "E304", {"start": v(-108.07, 5.1) * mm, "end": v(-118.37, 7.03) * mm});
            skLineSegment(sketch, "E305", {"start": v(-118.37, 7.03) * mm, "end": v(-119.69, 7.31) * mm});
            skLineSegment(sketch, "E306", {"start": v(-119.69, 7.31) * mm, "end": v(-120.26, 7.6) * mm});
            skLineSegment(sketch, "E307", {"start": v(-120.26, 7.6) * mm, "end": v(-121.58, 9.69) * mm});
            skLineSegment(sketch, "E308", {"start": v(-121.58, 9.69) * mm, "end": v(-114.1, 8.15) * mm});
            skLineSegment(sketch, "E309", {"start": v(-114.1, 8.15) * mm, "end": v(-108.53, 7.2) * mm});
            skLineSegment(sketch, "E310", {"start": v(-108.53, 7.2) * mm, "end": v(-102.21, 6.32) * mm});
            skLineSegment(sketch, "E311", {"start": v(-102.21, 6.32) * mm, "end": v(-97.2, 5.78) * mm});
            skLineSegment(sketch, "E312", {"start": v(-97.2, 5.78) * mm, "end": v(-91.32, 5.17) * mm});
            skLineSegment(sketch, "E313", {"start": v(-91.32, 5.17) * mm, "end": v(-86.25, 4.85) * mm});
            skLineSegment(sketch, "E314", {"start": v(-86.25, 4.85) * mm, "end": v(-80.05, 4.46) * mm});
            skLineSegment(sketch, "E315", {"start": v(-80.05, 4.46) * mm, "end": v(-75.13, 4.15) * mm});
            skLineSegment(sketch, "E316", {"start": v(-75.13, 4.15) * mm, "end": v(-65.5, 4.36) * mm});
            skLineSegment(sketch, "E317", {"start": v(-67.4, 3.28) * mm, "end": v(-74.3, 3.59) * mm});
            skLineSegment(sketch, "E318", {"start": v(-74.3, 3.59) * mm, "end": v(-82.93, 3.96) * mm});
            skLineSegment(sketch, "E319", {"start": v(-82.93, 3.96) * mm, "end": v(-86.54, 4.19) * mm});
            skLineSegment(sketch, "E320", {"start": v(-86.54, 4.19) * mm, "end": v(-90.92, 4.46) * mm});
            skLineSegment(sketch, "E321", {"start": v(-90.92, 4.46) * mm, "end": v(-94.51, 4.85) * mm});
            skLineSegment(sketch, "E322", {"start": v(-94.51, 4.85) * mm, "end": v(-98.3, 5.26) * mm});
            skLineSegment(sketch, "E323", {"start": v(-98.3, 5.26) * mm, "end": v(-104.8, 5.99) * mm});
            skLineSegment(sketch, "E324", {"start": v(-104.8, 5.99) * mm, "end": v(-109.5, 6.64) * mm});
            skLineSegment(sketch, "E325", {"start": v(-109.5, 6.64) * mm, "end": v(-115.26, 7.67) * mm});
            skLineSegment(sketch, "E326", {"start": v(-115.26, 7.67) * mm, "end": v(-119.16, 8.53) * mm});
            skLineSegment(sketch, "E327", {"start": v(-119.16, 8.53) * mm, "end": v(-121.58, 9.69) * mm});
            skLineSegment(sketch, "E328", {"start": v(55.1, 0.72) * mm, "end": v(77.18, 0.72) * mm});
            skLineSegment(sketch, "E329", {"start": v(77.18, 0.72) * mm, "end": v(78, 0.09) * mm});
            skLineSegment(sketch, "E330", {"start": v(78, 0.09) * mm, "end": v(78, -1.28) * mm});
            skLineSegment(sketch, "E331", {"start": v(78, -1.28) * mm, "end": v(77.18, -2.05) * mm});
            skLineSegment(sketch, "E332", {"start": v(77.18, -2.05) * mm, "end": v(55.1, -2.05) * mm});
            skLineSegment(sketch, "E333", {"start": v(54.05, 3.5) * mm, "end": v(55.1, 3.5) * mm});
            skLineSegment(sketch, "E334", {"start": v(55.1, 3.5) * mm, "end": v(55.1, -4.56) * mm});
            skLineSegment(sketch, "E335", {"start": v(55.1, -4.56) * mm, "end": v(54.05, -4.52) * mm});
            skLineSegment(sketch, "E336", {"start": v(54.05, -4.52) * mm, "end": v(54.05, 3.5) * mm});
            skLineSegment(sketch, "E337", {"start": v(56, -0.12) * mm, "end": v(55.47, -0.55) * mm});
            skLineSegment(sketch, "E338", {"start": v(55.47, -0.55) * mm, "end": v(56.05, -1.26) * mm});
            skLineSegment(sketch, "E339", {"start": v(56.05, -1.26) * mm, "end": v(56.52, -0.87) * mm});
            skLineSegment(sketch, "E340", {"start": v(56.52, -0.87) * mm, "end": v(56, -0.12) * mm});
            skLineSegment(sketch, "E341", {"start": v(57.31, -0.12) * mm, "end": v(56.81, -0.69) * mm});
            skLineSegment(sketch, "E342", {"start": v(56.81, -0.69) * mm, "end": v(57.49, -1.28) * mm});
            skLineSegment(sketch, "E343", {"start": v(57.49, -1.28) * mm, "end": v(57.85, -0.86) * mm});
            skLineSegment(sketch, "E344", {"start": v(57.85, -0.86) * mm, "end": v(57.31, -0.12) * mm});
            skLineSegment(sketch, "E345", {"start": v(58.7, -0.12) * mm, "end": v(58.15, -0.82) * mm});
            skLineSegment(sketch, "E346", {"start": v(58.15, -0.82) * mm, "end": v(58.8, -1.33) * mm});
            skLineSegment(sketch, "E347", {"start": v(58.8, -1.33) * mm, "end": v(59.22, -0.8) * mm});
            skLineSegment(sketch, "E348", {"start": v(59.22, -0.8) * mm, "end": v(58.7, -0.12) * mm});
            skLineSegment(sketch, "E349", {"start": v(60, -0.12) * mm, "end": v(59.56, -0.73) * mm});
            skLineSegment(sketch, "E350", {"start": v(59.56, -0.73) * mm, "end": v(59.95, -1.3) * mm});
            skLineSegment(sketch, "E351", {"start": v(59.95, -1.3) * mm, "end": v(60.38, -0.75) * mm});
            skLineSegment(sketch, "E352", {"start": v(60.38, -0.75) * mm, "end": v(60, -0.12) * mm});
            skLineSegment(sketch, "E353", {"start": v(61.32, -0.12) * mm, "end": v(60.84, -0.64) * mm});
            skLineSegment(sketch, "E354", {"start": v(60.84, -0.64) * mm, "end": v(61.3, -1.35) * mm});
            skLineSegment(sketch, "E355", {"start": v(61.3, -1.35) * mm, "end": v(61.84, -1) * mm});
            skLineSegment(sketch, "E356", {"start": v(61.84, -1) * mm, "end": v(61.32, -0.12) * mm});
            skLineSegment(sketch, "E357", {"start": v(62.64, -0.12) * mm, "end": v(62.11, -0.62) * mm});
            skLineSegment(sketch, "E358", {"start": v(62.11, -0.62) * mm, "end": v(62.73, -1.26) * mm});
            skLineSegment(sketch, "E359", {"start": v(62.73, -1.26) * mm, "end": v(63.16, -0.87) * mm});
            skLineSegment(sketch, "E360", {"start": v(63.16, -0.87) * mm, "end": v(62.64, -0.12) * mm});
            skLineSegment(sketch, "E361", {"start": v(63.96, -0.12) * mm, "end": v(63.46, -0.55) * mm});
            skLineSegment(sketch, "E362", {"start": v(63.46, -0.55) * mm, "end": v(64, -1.18) * mm});
            skLineSegment(sketch, "E363", {"start": v(64, -1.18) * mm, "end": v(64.39, -0.85) * mm});
            skLineSegment(sketch, "E364", {"start": v(64.39, -0.85) * mm, "end": v(63.96, -0.12) * mm});
            skLineSegment(sketch, "E365", {"start": v(65.37, -0.12) * mm, "end": v(64.85, -0.64) * mm});
            skLineSegment(sketch, "E366", {"start": v(64.85, -0.64) * mm, "end": v(65.38, -1.18) * mm});
            skLineSegment(sketch, "E367", {"start": v(65.38, -1.18) * mm, "end": v(65.78, -0.85) * mm});
            skLineSegment(sketch, "E368", {"start": v(65.78, -0.85) * mm, "end": v(65.37, -0.12) * mm});
            skLineSegment(sketch, "E369", {"start": v(66.76, -0.07) * mm, "end": v(66.21, -0.55) * mm});
            skLineSegment(sketch, "E370", {"start": v(66.21, -0.55) * mm, "end": v(66.77, -1.19) * mm});
            skLineSegment(sketch, "E371", {"start": v(66.77, -1.19) * mm, "end": v(67.22, -0.8) * mm});
            skLineSegment(sketch, "E372", {"start": v(67.22, -0.8) * mm, "end": v(66.76, -0.07) * mm});
            skLineSegment(sketch, "E373", {"start": v(68.17, -0.12) * mm, "end": v(67.55, -0.57) * mm});
            skLineSegment(sketch, "E374", {"start": v(67.55, -0.57) * mm, "end": v(67.98, -1.15) * mm});
            skLineSegment(sketch, "E375", {"start": v(67.98, -1.15) * mm, "end": v(68.47, -0.78) * mm});
            skLineSegment(sketch, "E376", {"start": v(68.47, -0.78) * mm, "end": v(68.17, -0.12) * mm});
            skLineSegment(sketch, "E377", {"start": v(69.4, -0.12) * mm, "end": v(68.8, -0.64) * mm});
            skLineSegment(sketch, "E378", {"start": v(68.8, -0.64) * mm, "end": v(69.17, -1.32) * mm});
            skLineSegment(sketch, "E379", {"start": v(69.17, -1.32) * mm, "end": v(69.85, -0.96) * mm});
            skLineSegment(sketch, "E380", {"start": v(69.85, -0.96) * mm, "end": v(69.4, -0.12) * mm});
            skLineSegment(sketch, "E381", {"start": v(70.7, -0.12) * mm, "end": v(70.06, -0.6) * mm});
            skLineSegment(sketch, "E382", {"start": v(70.06, -0.6) * mm, "end": v(70.51, -1.2) * mm});
            skLineSegment(sketch, "E383", {"start": v(70.51, -1.2) * mm, "end": v(71.06, -0.79) * mm});
            skLineSegment(sketch, "E384", {"start": v(71.06, -0.79) * mm, "end": v(70.7, -0.12) * mm});
            skLineSegment(sketch, "E385", {"start": v(72.08, -0.12) * mm, "end": v(71.47, -0.64) * mm});
            skLineSegment(sketch, "E386", {"start": v(71.47, -0.64) * mm, "end": v(72, -1.26) * mm});
            skLineSegment(sketch, "E387", {"start": v(72, -1.26) * mm, "end": v(72.5, -0.83) * mm});
            skLineSegment(sketch, "E388", {"start": v(72.5, -0.83) * mm, "end": v(72.08, -0.12) * mm});
            skLineSegment(sketch, "E389", {"start": v(73.47, -0.12) * mm, "end": v(72.83, -0.48) * mm});
            skLineSegment(sketch, "E390", {"start": v(72.83, -0.48) * mm, "end": v(73.22, -1.17) * mm});
            skLineSegment(sketch, "E391", {"start": v(73.22, -1.17) * mm, "end": v(73.76, -0.86) * mm});
            skLineSegment(sketch, "E392", {"start": v(73.76, -0.86) * mm, "end": v(73.47, -0.12) * mm});
            skLineSegment(sketch, "E393", {"start": v(74.75, -0.13) * mm, "end": v(74.1, -0.48) * mm});
            skLineSegment(sketch, "E394", {"start": v(74.1, -0.48) * mm, "end": v(74.5, -1.18) * mm});
            skLineSegment(sketch, "E395", {"start": v(74.5, -1.18) * mm, "end": v(75.08, -0.86) * mm});
            skLineSegment(sketch, "E396", {"start": v(75.08, -0.86) * mm, "end": v(74.75, -0.13) * mm});
            skPoint(sketch, "E397.orphan", {"position": v(74.77, -0.12) * mm});
            skLineSegment(sketch, "E398", {"start": v(76.04, -0.05) * mm, "end": v(75.53, -0.49) * mm});
            skPoint(sketch, "E398.endSnap0", {"position": v(73.62, -0.49) * mm});
            skLineSegment(sketch, "E399", {"start": v(75.53, -0.49) * mm, "end": v(75.88, -1.29) * mm});
            skLineSegment(sketch, "E400", {"start": v(75.88, -1.29) * mm, "end": v(76.48, -0.78) * mm});
            skLineSegment(sketch, "E401", {"start": v(76.48, -0.78) * mm, "end": v(76.04, -0.05) * mm});
            skLineSegment(sketch, "E402", {"start": v(54.05, 0.72) * mm, "end": v(52.14, -0.36) * mm});
            skLineSegment(sketch, "E403", {"start": v(52.14, -0.36) * mm, "end": v(54.05, -2.05) * mm});
            skLineSegment(sketch, "E404", {"start": v(54.05, -2.05) * mm, "end": v(51.12, -2.05) * mm});
            skLineSegment(sketch, "E405", {"start": v(51.12, -2.05) * mm, "end": v(42.86, -1.74) * mm});
            skLineSegment(sketch, "E406", {"start": v(42.86, -1.74) * mm, "end": v(36.2, -1.32) * mm});
            skLineSegment(sketch, "E407", {"start": v(36.2, -1.32) * mm, "end": v(25.62, -0.42) * mm});
            skLineSegment(sketch, "E408", {"start": v(25.62, -0.42) * mm, "end": v(11.47, 1.45) * mm});
            skLineSegment(sketch, "E409", {"start": v(11.47, 1.45) * mm, "end": v(1.18, 3.38) * mm});
            skLineSegment(sketch, "E410", {"start": v(1.18, 3.38) * mm, "end": v(-0.14, 3.67) * mm});
            skLineSegment(sketch, "E411", {"start": v(-0.14, 3.67) * mm, "end": v(-0.72, 3.96) * mm});
            skLineSegment(sketch, "E412", {"start": v(-0.72, 3.96) * mm, "end": v(-2.04, 6.05) * mm});
            skLineSegment(sketch, "E413", {"start": v(-2.04, 6.05) * mm, "end": v(5.44, 4.51) * mm});
            skLineSegment(sketch, "E414", {"start": v(5.44, 4.51) * mm, "end": v(11.01, 3.56) * mm});
            skLineSegment(sketch, "E415", {"start": v(11.01, 3.56) * mm, "end": v(17.33, 2.68) * mm});
            skLineSegment(sketch, "E416", {"start": v(17.33, 2.68) * mm, "end": v(22.34, 2.14) * mm});
            skLineSegment(sketch, "E417", {"start": v(22.34, 2.14) * mm, "end": v(28.22, 1.53) * mm});
            skLineSegment(sketch, "E418", {"start": v(28.22, 1.53) * mm, "end": v(33.3, 1.2) * mm});
            skLineSegment(sketch, "E419", {"start": v(33.3, 1.2) * mm, "end": v(39.49, 0.82) * mm});
            skLineSegment(sketch, "E420", {"start": v(39.49, 0.82) * mm, "end": v(44.41, 0.5) * mm});
            skLineSegment(sketch, "E421", {"start": v(44.41, 0.5) * mm, "end": v(54.05, 0.72) * mm});
            skLineSegment(sketch, "E422", {"start": v(52.14, -0.36) * mm, "end": v(45.24, -0.05) * mm});
            skLineSegment(sketch, "E423", {"start": v(45.24, -0.05) * mm, "end": v(36.6, 0.32) * mm});
            skLineSegment(sketch, "E424", {"start": v(36.6, 0.32) * mm, "end": v(33, 0.55) * mm});
            skLineSegment(sketch, "E425", {"start": v(33, 0.55) * mm, "end": v(28.62, 0.82) * mm});
            skLineSegment(sketch, "E426", {"start": v(28.62, 0.82) * mm, "end": v(25.03, 1.2) * mm});
            skLineSegment(sketch, "E427", {"start": v(25.03, 1.2) * mm, "end": v(21.24, 1.62) * mm});
            skLineSegment(sketch, "E428", {"start": v(21.24, 1.62) * mm, "end": v(14.75, 2.35) * mm});
            skLineSegment(sketch, "E429", {"start": v(14.75, 2.35) * mm, "end": v(10.04, 3) * mm});
            skLineSegment(sketch, "E430", {"start": v(10.04, 3) * mm, "end": v(4.28, 4.03) * mm});
            skLineSegment(sketch, "E431", {"start": v(4.28, 4.03) * mm, "end": v(0.38, 4.9) * mm});
            skLineSegment(sketch, "E432", {"start": v(0.38, 4.9) * mm, "end": v(-2.04, 6.05) * mm});
            skSolve(sketch);
        }
        {
            var Q0;
            Q0 = qSketchRegion(id + "F7", true);
            extrude(context, id + "F8", {"entities" : qUnion([Q0]), "operationType" : NewBodyOperationType.ADD, "depth" : 1.27 * mm, "offsetDistance" : 25.4 * mm});
        }
        {
            var Q0;
            Q0=makeQuery(id+"F8.opExtrude","SWEPT_BODY",BODY,{"disambiguationData":[OSD([sQuery(id+"F7.wireOp",EDGE,"E223"),sQuery(id+"F7.wireOp",EDGE,"E224"),sQuery(id+"F7.wireOp",EDGE,"E225"),sQuery(id+"F7.wireOp",EDGE,"E226"),sQuery(id+"F7.wireOp",EDGE,"E227"),sQuery(id+"F7.wireOp",EDGE,"E228"),sQuery(id+"F7.wireOp",EDGE,"E229"),sQuery(id+"F7.wireOp",EDGE,"E230"),sQuery(id+"F7.wireOp",EDGE,"E231"),sQuery(id+"F7.wireOp",EDGE,"E232"),sQuery(id+"F7.wireOp",EDGE,"E233"),sQuery(id+"F7.wireOp",EDGE,"E234"),sQuery(id+"F7.wireOp",EDGE,"E235"),sQuery(id+"F7.wireOp",EDGE,"E236"),sQuery(id+"F7.wireOp",EDGE,"E237"),sQuery(id+"F7.wireOp",EDGE,"E238"),sQuery(id+"F7.wireOp",EDGE,"E239"),sQuery(id+"F7.wireOp",EDGE,"E240"),sQuery(id+"F7.wireOp",EDGE,"E241"),sQuery(id+"F7.wireOp",EDGE,"E242"),sQuery(id+"F7.wireOp",EDGE,"E243"),sQuery(id+"F7.wireOp",EDGE,"E244"),sQuery(id+"F7.wireOp",EDGE,"E245"),sQuery(id+"F7.wireOp",EDGE,"E246"),sQuery(id+"F7.wireOp",EDGE,"E247"),sQuery(id+"F7.wireOp",EDGE,"E248"),sQuery(id+"F7.wireOp",EDGE,"E249"),sQuery(id+"F7.wireOp",EDGE,"E250"),sQuery(id+"F7.wireOp",EDGE,"E251"),sQuery(id+"F7.wireOp",EDGE,"E252"),sQuery(id+"F7.wireOp",EDGE,"E253"),sQuery(id+"F7.wireOp",EDGE,"E254"),sQuery(id+"F7.wireOp",EDGE,"E255"),sQuery(id+"F7.wireOp",EDGE,"E256"),sQuery(id+"F7.wireOp",EDGE,"E257"),sQuery(id+"F7.wireOp",EDGE,"E258"),sQuery(id+"F7.wireOp",EDGE,"E259"),sQuery(id+"F7.wireOp",EDGE,"E260"),sQuery(id+"F7.wireOp",EDGE,"E261"),sQuery(id+"F7.wireOp",EDGE,"E262"),sQuery(id+"F7.wireOp",EDGE,"E263"),sQuery(id+"F7.wireOp",EDGE,"E264"),sQuery(id+"F7.wireOp",EDGE,"E265"),sQuery(id+"F7.wireOp",EDGE,"E266"),sQuery(id+"F7.wireOp",EDGE,"E267"),sQuery(id+"F7.wireOp",EDGE,"E268"),sQuery(id+"F7.wireOp",EDGE,"E269"),sQuery(id+"F7.wireOp",EDGE,"E270"),sQuery(id+"F7.wireOp",EDGE,"E271"),sQuery(id+"F7.wireOp",EDGE,"E272"),sQuery(id+"F7.wireOp",EDGE,"E273"),sQuery(id+"F7.wireOp",EDGE,"E274"),sQuery(id+"F7.wireOp",EDGE,"E275"),sQuery(id+"F7.wireOp",EDGE,"E276"),sQuery(id+"F7.wireOp",EDGE,"E277"),sQuery(id+"F7.wireOp",EDGE,"E278"),sQuery(id+"F7.wireOp",EDGE,"E279"),sQuery(id+"F7.wireOp",EDGE,"E280"),sQuery(id+"F7.wireOp",EDGE,"E281"),sQuery(id+"F7.wireOp",EDGE,"E282"),sQuery(id+"F7.wireOp",EDGE,"E283"),sQuery(id+"F7.wireOp",EDGE,"E284"),sQuery(id+"F7.wireOp",EDGE,"E285"),sQuery(id+"F7.wireOp",EDGE,"E286"),sQuery(id+"F7.wireOp",EDGE,"E287"),sQuery(id+"F7.wireOp",EDGE,"E288"),sQuery(id+"F7.wireOp",EDGE,"E289"),sQuery(id+"F7.wireOp",EDGE,"E290"),sQuery(id+"F7.wireOp",EDGE,"E291"),sQuery(id+"F7.wireOp",EDGE,"E293"),sQuery(id+"F7.wireOp",EDGE,"E294"),sQuery(id+"F7.wireOp",EDGE,"E295"),sQuery(id+"F7.wireOp",EDGE,"E296"),sQuery(id+"F7.wireOp",EDGE,"E299"),sQuery(id+"F7.wireOp",EDGE,"E300"),sQuery(id+"F7.wireOp",EDGE,"E301"),sQuery(id+"F7.wireOp",EDGE,"E302"),sQuery(id+"F7.wireOp",EDGE,"E303"),sQuery(id+"F7.wireOp",EDGE,"E304"),sQuery(id+"F7.wireOp",EDGE,"E305"),sQuery(id+"F7.wireOp",EDGE,"E306"),sQuery(id+"F7.wireOp",EDGE,"E307"),sQuery(id+"F7.wireOp",EDGE,"E308"),sQuery(id+"F7.wireOp",EDGE,"E309"),sQuery(id+"F7.wireOp",EDGE,"E310"),sQuery(id+"F7.wireOp",EDGE,"E311"),sQuery(id+"F7.wireOp",EDGE,"E312"),sQuery(id+"F7.wireOp",EDGE,"E313"),sQuery(id+"F7.wireOp",EDGE,"E314"),sQuery(id+"F7.wireOp",EDGE,"E315"),sQuery(id+"F7.wireOp",EDGE,"E316")])]});
            deleteBodies(context, id + "F9", {"entities" : qUnion([Q0])});
        }
        {
            var Q0;
            Q0=qCreatedBy(makeId("Top.planeOp"),FACE);
            var sketch = newSketch(context, id + "F10", { "sketchPlane" : qUnion([Q0])});
            skLineSegment(sketch, "E433", {"start": v(18.4, -3.92) * mm, "end": v(17.77, -6.53) * mm});
            skLineSegment(sketch, "E434", {"start": v(17.77, -6.53) * mm, "end": v(17.96, -9.26) * mm});
            skLineSegment(sketch, "E435", {"start": v(17.96, -9.26) * mm, "end": v(18.63, -12.63) * mm});
            skLineSegment(sketch, "E436", {"start": v(18.63, -12.63) * mm, "end": v(19.24, -14.43) * mm});
            skLineSegment(sketch, "E437", {"start": v(19.24, -14.43) * mm, "end": v(20.58, -11.89) * mm});
            skLineSegment(sketch, "E438", {"start": v(20.58, -11.89) * mm, "end": v(22.54, -9.51) * mm});
            skLineSegment(sketch, "E439", {"start": v(22.54, -9.51) * mm, "end": v(25.27, -7.4) * mm});
            skLineSegment(sketch, "E440", {"start": v(25.27, -7.4) * mm, "end": v(27.47, -5.41) * mm});
            skLineSegment(sketch, "E441", {"start": v(27.47, -5.41) * mm, "end": v(24.7, -8.6) * mm});
            skLineSegment(sketch, "E442", {"start": v(24.7, -8.6) * mm, "end": v(23.6, -10.26) * mm});
            skLineSegment(sketch, "E443", {"start": v(23.6, -10.26) * mm, "end": v(22.86, -12.15) * mm});
            skLineSegment(sketch, "E444", {"start": v(22.86, -12.15) * mm, "end": v(22.65, -14.01) * mm});
            skLineSegment(sketch, "E445", {"start": v(22.65, -14.01) * mm, "end": v(22.94, -16.12) * mm});
            skLineSegment(sketch, "E446", {"start": v(22.94, -16.12) * mm, "end": v(24, -18.8) * mm});
            skLineSegment(sketch, "E447", {"start": v(24, -18.8) * mm, "end": v(24.7, -20.77) * mm});
            skLineSegment(sketch, "E448", {"start": v(24.7, -20.77) * mm, "end": v(24.9, -22.27) * mm});
            skLineSegment(sketch, "E449", {"start": v(24.9, -22.27) * mm, "end": v(24.58, -23.93) * mm});
            skLineSegment(sketch, "E450", {"start": v(24.58, -23.93) * mm, "end": v(23.75, -26.03) * mm});
            skLineSegment(sketch, "E451", {"start": v(23.75, -26.03) * mm, "end": v(22.44, -27.23) * mm});
            skLineSegment(sketch, "E452", {"start": v(22.44, -27.23) * mm, "end": v(18.57, -29.16) * mm});
            skLineSegment(sketch, "E453", {"start": v(18.57, -29.16) * mm, "end": v(14.9, -28.36) * mm});
            skLineSegment(sketch, "E454", {"start": v(14.9, -28.36) * mm, "end": v(12.17, -27.89) * mm});
            skLineSegment(sketch, "E455", {"start": v(12.17, -27.89) * mm, "end": v(10.62, -27.07) * mm});
            skLineSegment(sketch, "E456", {"start": v(10.62, -27.07) * mm, "end": v(9.5, -25.38) * mm});
            skLineSegment(sketch, "E457", {"start": v(9.71, -25.95) * mm, "end": v(9.5, -25.38) * mm});
            skLineSegment(sketch, "E458", {"start": v(9.71, -25.95) * mm, "end": v(9.71, -15.05) * mm});
            skLineSegment(sketch, "E459", {"start": v(9.46, -15.94) * mm, "end": v(9.71, -15.05) * mm});
            skLineSegment(sketch, "E460", {"start": v(9.46, -15.94) * mm, "end": v(9.87, -13.32) * mm});
            skLineSegment(sketch, "E461", {"start": v(9.87, -13.32) * mm, "end": v(9.92, -10.82) * mm});
            skLineSegment(sketch, "E462", {"start": v(9.92, -10.82) * mm, "end": v(9.71, -8.34) * mm});
            skLineSegment(sketch, "E463", {"start": v(9.71, -8.34) * mm, "end": v(11.28, -10.5) * mm});
            skLineSegment(sketch, "E464", {"start": v(11.28, -10.5) * mm, "end": v(12.79, -13.66) * mm});
            skLineSegment(sketch, "E465", {"start": v(12.79, -13.66) * mm, "end": v(14.15, -16.98) * mm});
            skLineSegment(sketch, "E466", {"start": v(14.15, -16.98) * mm, "end": v(14.92, -12.68) * mm});
            skLineSegment(sketch, "E467", {"start": v(14.92, -12.68) * mm, "end": v(16.15, -8.22) * mm});
            skLineSegment(sketch, "E468", {"start": v(16.15, -8.22) * mm, "end": v(17.45, -4.93) * mm});
            skLineSegment(sketch, "E469", {"start": v(17.45, -4.93) * mm, "end": v(18.4, -3.92) * mm});
            skLineSegment(sketch, "E470", {"start": v(17.25, -8.9) * mm, "end": v(17.03, -12.4) * mm});
            skLineSegment(sketch, "E471", {"start": v(17.03, -12.4) * mm, "end": v(17.2, -14.86) * mm});
            skLineSegment(sketch, "E472", {"start": v(17.2, -14.86) * mm, "end": v(17.84, -17.3) * mm});
            skLineSegment(sketch, "E473", {"start": v(17.84, -17.3) * mm, "end": v(18.97, -19.1) * mm});
            skLineSegment(sketch, "E474", {"start": v(18.97, -19.1) * mm, "end": v(20.15, -15.66) * mm});
            skLineSegment(sketch, "E475", {"start": v(20.15, -15.66) * mm, "end": v(21.28, -13.73) * mm});
            skLineSegment(sketch, "E476", {"start": v(21.28, -13.73) * mm, "end": v(21.95, -13.02) * mm});
            skLineSegment(sketch, "E477", {"start": v(21.95, -13.02) * mm, "end": v(21.45, -14.74) * mm});
            skLineSegment(sketch, "E478", {"start": v(21.45, -14.74) * mm, "end": v(21.45, -16.81) * mm});
            skLineSegment(sketch, "E479", {"start": v(21.45, -16.81) * mm, "end": v(21.84, -18.75) * mm});
            skLineSegment(sketch, "E480", {"start": v(21.84, -18.75) * mm, "end": v(22.45, -21) * mm});
            skLineSegment(sketch, "E481", {"start": v(22.45, -21) * mm, "end": v(23.1, -23.03) * mm});
            skLineSegment(sketch, "E482", {"start": v(23.1, -23.03) * mm, "end": v(23.25, -24.58) * mm});
            skLineSegment(sketch, "E483", {"start": v(23.25, -24.58) * mm, "end": v(22.97, -26.11) * mm});
            skLineSegment(sketch, "E484", {"start": v(22.97, -26.11) * mm, "end": v(21.95, -27.32) * mm});
            skLineSegment(sketch, "E485", {"start": v(21.95, -27.32) * mm, "end": v(18.57, -29.19) * mm});
            skLineSegment(sketch, "E486", {"start": v(18.57, -29.19) * mm, "end": v(14.41, -28.06) * mm});
            skLineSegment(sketch, "E487", {"start": v(14.41, -28.06) * mm, "end": v(12.08, -26.76) * mm});
            skLineSegment(sketch, "E488", {"start": v(12.08, -26.76) * mm, "end": v(10.41, -24.52) * mm});
            skLineSegment(sketch, "E489", {"start": v(10.41, -24.52) * mm, "end": v(10.08, -22.85) * mm});
            skLineSegment(sketch, "E490", {"start": v(10.08, -22.85) * mm, "end": v(10.6, -21.02) * mm});
            skLineSegment(sketch, "E491", {"start": v(10.6, -21.02) * mm, "end": v(11.33, -18.49) * mm});
            skLineSegment(sketch, "E492", {"start": v(11.33, -18.49) * mm, "end": v(11.49, -16.2) * mm});
            skLineSegment(sketch, "E493", {"start": v(11.49, -16.2) * mm, "end": v(11.38, -14.65) * mm});
            skLineSegment(sketch, "E494", {"start": v(11.38, -14.65) * mm, "end": v(12.54, -16.98) * mm});
            skLineSegment(sketch, "E495", {"start": v(12.54, -16.98) * mm, "end": v(13.82, -20.04) * mm});
            skLineSegment(sketch, "E496", {"start": v(13.82, -20.04) * mm, "end": v(14.4, -21.19) * mm});
            skLineSegment(sketch, "E497", {"start": v(14.4, -21.19) * mm, "end": v(15, -17.88) * mm});
            skLineSegment(sketch, "E498", {"start": v(15, -17.88) * mm, "end": v(15.98, -13.32) * mm});
            skLineSegment(sketch, "E499", {"start": v(15.98, -13.32) * mm, "end": v(16.54, -11.3) * mm});
            skLineSegment(sketch, "E500", {"start": v(16.54, -11.3) * mm, "end": v(17.25, -8.9) * mm});
            skLineSegment(sketch, "E501", {"start": v(16.69, -16.26) * mm, "end": v(16.62, -17.1) * mm});
            skLineSegment(sketch, "E502", {"start": v(16.62, -17.1) * mm, "end": v(16.73, -18.33) * mm});
            skLineSegment(sketch, "E503", {"start": v(16.73, -18.33) * mm, "end": v(17.22, -20.2) * mm});
            skLineSegment(sketch, "E504", {"start": v(17.22, -20.2) * mm, "end": v(18.64, -23.02) * mm});
            skLineSegment(sketch, "E505", {"start": v(18.64, -23.02) * mm, "end": v(19.29, -20.66) * mm});
            skLineSegment(sketch, "E506", {"start": v(19.29, -20.66) * mm, "end": v(19.87, -19.53) * mm});
            skLineSegment(sketch, "E507", {"start": v(19.87, -19.53) * mm, "end": v(20.76, -18.63) * mm});
            skLineSegment(sketch, "E508", {"start": v(20.76, -18.63) * mm, "end": v(20.44, -19.44) * mm});
            skLineSegment(sketch, "E509", {"start": v(20.44, -19.44) * mm, "end": v(20.37, -20.52) * mm});
            skLineSegment(sketch, "E510", {"start": v(20.37, -20.52) * mm, "end": v(20.64, -21.89) * mm});
            skLineSegment(sketch, "E511", {"start": v(20.64, -21.89) * mm, "end": v(21.26, -23.49) * mm});
            skLineSegment(sketch, "E512", {"start": v(21.26, -23.49) * mm, "end": v(21.74, -24.74) * mm});
            skLineSegment(sketch, "E513", {"start": v(21.74, -24.74) * mm, "end": v(22.06, -25.39) * mm});
            skLineSegment(sketch, "E514", {"start": v(22.06, -25.39) * mm, "end": v(21.8, -26.06) * mm});
            skLineSegment(sketch, "E515", {"start": v(21.8, -26.06) * mm, "end": v(20.48, -27.86) * mm});
            skLineSegment(sketch, "E516", {"start": v(20.48, -27.86) * mm, "end": v(18.57, -28.82) * mm});
            skLineSegment(sketch, "E517", {"start": v(18.57, -28.82) * mm, "end": v(14.37, -27.43) * mm});
            skLineSegment(sketch, "E518", {"start": v(14.37, -27.43) * mm, "end": v(12.84, -26.38) * mm});
            skLineSegment(sketch, "E519", {"start": v(12.84, -26.38) * mm, "end": v(12.03, -25.2) * mm});
            skLineSegment(sketch, "E520", {"start": v(12.03, -25.2) * mm, "end": v(11.63, -23.64) * mm});
            skLineSegment(sketch, "E521", {"start": v(11.63, -23.64) * mm, "end": v(11.9, -21.9) * mm});
            skLineSegment(sketch, "E522", {"start": v(11.9, -21.9) * mm, "end": v(12.28, -20.04) * mm});
            skLineSegment(sketch, "E523", {"start": v(12.28, -20.04) * mm, "end": v(12.28, -18.67) * mm});
            skLineSegment(sketch, "E524", {"start": v(12.28, -18.67) * mm, "end": v(13.02, -20.17) * mm});
            skLineSegment(sketch, "E525", {"start": v(13.02, -20.17) * mm, "end": v(13.95, -21.44) * mm});
            skLineSegment(sketch, "E526", {"start": v(13.95, -21.44) * mm, "end": v(15.41, -23.17) * mm});
            skLineSegment(sketch, "E527", {"start": v(15.41, -23.17) * mm, "end": v(15.57, -20.63) * mm});
            skLineSegment(sketch, "E528", {"start": v(15.57, -20.63) * mm, "end": v(15.88, -18.55) * mm});
            skLineSegment(sketch, "E529", {"start": v(15.88, -18.55) * mm, "end": v(16.35, -16.89) * mm});
            skLineSegment(sketch, "E530", {"start": v(16.35, -16.89) * mm, "end": v(16.69, -16.26) * mm});
            skLineSegment(sketch, "E531", {"start": v(20.28, -22.87) * mm, "end": v(20.21, -23.89) * mm});
            skLineSegment(sketch, "E532", {"start": v(20.21, -23.89) * mm, "end": v(20.53, -25.48) * mm});
            skLineSegment(sketch, "E533", {"start": v(20.53, -25.48) * mm, "end": v(20.84, -26.65) * mm});
            skLineSegment(sketch, "E534", {"start": v(20.84, -26.65) * mm, "end": v(20.67, -27.6) * mm});
            skLineSegment(sketch, "E535", {"start": v(20.67, -27.6) * mm, "end": v(18.57, -28.66) * mm});
            skLineSegment(sketch, "E536", {"start": v(18.57, -28.66) * mm, "end": v(15.87, -27.71) * mm});
            skLineSegment(sketch, "E537", {"start": v(15.87, -27.71) * mm, "end": v(14.24, -26.83) * mm});
            skLineSegment(sketch, "E538", {"start": v(14.24, -26.83) * mm, "end": v(13.42, -26.1) * mm});
            skLineSegment(sketch, "E539", {"start": v(13.42, -26.1) * mm, "end": v(13.07, -25.41) * mm});
            skLineSegment(sketch, "E540", {"start": v(13.07, -25.41) * mm, "end": v(12.98, -24.02) * mm});
            skLineSegment(sketch, "E541", {"start": v(12.98, -24.02) * mm, "end": v(12.98, -22.68) * mm});
            skLineSegment(sketch, "E542", {"start": v(12.98, -22.68) * mm, "end": v(12.55, -21.55) * mm});
            skLineSegment(sketch, "E543", {"start": v(12.55, -21.55) * mm, "end": v(13.63, -22.81) * mm});
            skLineSegment(sketch, "E544", {"start": v(13.63, -22.81) * mm, "end": v(15.81, -25.03) * mm});
            skLineSegment(sketch, "E545", {"start": v(15.81, -25.03) * mm, "end": v(16.5, -25.54) * mm});
            skLineSegment(sketch, "E546", {"start": v(16.5, -25.54) * mm, "end": v(16.6, -23.92) * mm});
            skLineSegment(sketch, "E547", {"start": v(16.6, -23.92) * mm, "end": v(16.95, -22.66) * mm});
            skLineSegment(sketch, "E548", {"start": v(16.95, -22.66) * mm, "end": v(17.25, -24.17) * mm});
            skLineSegment(sketch, "E549", {"start": v(17.25, -24.17) * mm, "end": v(17.8, -25.28) * mm});
            skLineSegment(sketch, "E550", {"start": v(17.8, -25.28) * mm, "end": v(18.73, -26.63) * mm});
            skLineSegment(sketch, "E551", {"start": v(18.73, -26.63) * mm, "end": v(18.89, -24.74) * mm});
            skLineSegment(sketch, "E552", {"start": v(18.89, -24.74) * mm, "end": v(19.31, -23.66) * mm});
            skLineSegment(sketch, "E553", {"start": v(19.31, -23.66) * mm, "end": v(20.28, -22.87) * mm});
            skLineSegment(sketch, "E554", {"start": v(58.37, -5.84) * mm, "end": v(57.74, -8.44) * mm});
            skLineSegment(sketch, "E555", {"start": v(57.74, -8.44) * mm, "end": v(57.93, -11.18) * mm});
            skLineSegment(sketch, "E556", {"start": v(57.93, -11.18) * mm, "end": v(58.6, -14.55) * mm});
            skLineSegment(sketch, "E557", {"start": v(58.6, -14.55) * mm, "end": v(59.2, -16.34) * mm});
            skLineSegment(sketch, "E558", {"start": v(59.2, -16.34) * mm, "end": v(60.55, -13.8) * mm});
            skLineSegment(sketch, "E559", {"start": v(60.55, -13.8) * mm, "end": v(62.5, -11.43) * mm});
            skLineSegment(sketch, "E560", {"start": v(62.5, -11.43) * mm, "end": v(65.24, -9.32) * mm});
            skLineSegment(sketch, "E561", {"start": v(65.24, -9.32) * mm, "end": v(67.43, -7.33) * mm});
            skLineSegment(sketch, "E562", {"start": v(67.43, -7.33) * mm, "end": v(64.66, -10.5) * mm});
            skLineSegment(sketch, "E563", {"start": v(64.66, -10.5) * mm, "end": v(63.57, -12.17) * mm});
            skLineSegment(sketch, "E564", {"start": v(63.57, -12.17) * mm, "end": v(62.83, -14.07) * mm});
            skLineSegment(sketch, "E565", {"start": v(62.83, -14.07) * mm, "end": v(62.61, -15.92) * mm});
            skLineSegment(sketch, "E566", {"start": v(62.61, -15.92) * mm, "end": v(62.9, -18.03) * mm});
            skLineSegment(sketch, "E567", {"start": v(62.9, -18.03) * mm, "end": v(63.97, -20.7) * mm});
            skLineSegment(sketch, "E568", {"start": v(63.97, -20.7) * mm, "end": v(64.66, -22.68) * mm});
            skLineSegment(sketch, "E569", {"start": v(64.66, -22.68) * mm, "end": v(64.86, -24.18) * mm});
            skLineSegment(sketch, "E570", {"start": v(64.86, -24.18) * mm, "end": v(64.54, -25.84) * mm});
            skLineSegment(sketch, "E571", {"start": v(64.54, -25.84) * mm, "end": v(63.71, -27.94) * mm});
            skLineSegment(sketch, "E572", {"start": v(63.71, -27.94) * mm, "end": v(62.4, -29.14) * mm});
            skLineSegment(sketch, "E573", {"start": v(62.4, -29.14) * mm, "end": v(58.53, -31.08) * mm});
            skLineSegment(sketch, "E574", {"start": v(58.53, -31.08) * mm, "end": v(54.87, -30.28) * mm});
            skLineSegment(sketch, "E575", {"start": v(54.87, -30.28) * mm, "end": v(52.14, -29.8) * mm});
            skLineSegment(sketch, "E576", {"start": v(52.14, -29.8) * mm, "end": v(50.59, -28.98) * mm});
            skLineSegment(sketch, "E577", {"start": v(50.59, -28.98) * mm, "end": v(49.47, -27.3) * mm});
            skLineSegment(sketch, "E578", {"start": v(49.68, -27.86) * mm, "end": v(49.47, -27.3) * mm});
            skLineSegment(sketch, "E579", {"start": v(49.68, -27.86) * mm, "end": v(49.68, -16.97) * mm});
            skLineSegment(sketch, "E580", {"start": v(49.43, -17.85) * mm, "end": v(49.68, -16.97) * mm});
            skLineSegment(sketch, "E581", {"start": v(49.43, -17.85) * mm, "end": v(49.84, -15.23) * mm});
            skLineSegment(sketch, "E582", {"start": v(49.84, -15.23) * mm, "end": v(49.88, -12.73) * mm});
            skLineSegment(sketch, "E583", {"start": v(49.88, -12.73) * mm, "end": v(49.68, -10.25) * mm});
            skLineSegment(sketch, "E584", {"start": v(49.68, -10.25) * mm, "end": v(51.25, -12.41) * mm});
            skLineSegment(sketch, "E585", {"start": v(51.25, -12.41) * mm, "end": v(52.75, -15.57) * mm});
            skLineSegment(sketch, "E586", {"start": v(52.75, -15.57) * mm, "end": v(54.12, -18.9) * mm});
            skLineSegment(sketch, "E587", {"start": v(54.12, -18.9) * mm, "end": v(54.89, -14.6) * mm});
            skLineSegment(sketch, "E588", {"start": v(54.89, -14.6) * mm, "end": v(56.12, -10.13) * mm});
            skLineSegment(sketch, "E589", {"start": v(56.12, -10.13) * mm, "end": v(57.42, -6.84) * mm});
            skLineSegment(sketch, "E590", {"start": v(57.42, -6.84) * mm, "end": v(58.37, -5.84) * mm});
            skLineSegment(sketch, "E591", {"start": v(57.21, -10.82) * mm, "end": v(57, -14.3) * mm});
            skLineSegment(sketch, "E592", {"start": v(57, -14.3) * mm, "end": v(57.17, -16.77) * mm});
            skLineSegment(sketch, "E593", {"start": v(57.17, -16.77) * mm, "end": v(57.8, -19.2) * mm});
            skLineSegment(sketch, "E594", {"start": v(57.8, -19.2) * mm, "end": v(58.93, -21.02) * mm});
            skLineSegment(sketch, "E595", {"start": v(58.93, -21.02) * mm, "end": v(60.12, -17.58) * mm});
            skLineSegment(sketch, "E596", {"start": v(60.12, -17.58) * mm, "end": v(61.25, -15.64) * mm});
            skLineSegment(sketch, "E597", {"start": v(61.25, -15.64) * mm, "end": v(61.92, -14.93) * mm});
            skLineSegment(sketch, "E598", {"start": v(61.92, -14.93) * mm, "end": v(61.42, -16.66) * mm});
            skLineSegment(sketch, "E599", {"start": v(61.42, -16.66) * mm, "end": v(61.42, -18.72) * mm});
            skLineSegment(sketch, "E600", {"start": v(61.42, -18.72) * mm, "end": v(61.8, -20.66) * mm});
            skLineSegment(sketch, "E601", {"start": v(61.8, -20.66) * mm, "end": v(62.41, -22.92) * mm});
            skLineSegment(sketch, "E602", {"start": v(62.41, -22.92) * mm, "end": v(63.06, -24.94) * mm});
            skLineSegment(sketch, "E603", {"start": v(63.06, -24.94) * mm, "end": v(63.22, -26.5) * mm});
            skLineSegment(sketch, "E604", {"start": v(63.22, -26.5) * mm, "end": v(62.93, -28.03) * mm});
            skLineSegment(sketch, "E605", {"start": v(62.93, -28.03) * mm, "end": v(61.92, -29.23) * mm});
            skLineSegment(sketch, "E606", {"start": v(61.92, -29.23) * mm, "end": v(58.53, -31.1) * mm});
            skLineSegment(sketch, "E607", {"start": v(58.53, -31.1) * mm, "end": v(54.38, -29.97) * mm});
            skLineSegment(sketch, "E608", {"start": v(54.38, -29.97) * mm, "end": v(52.04, -28.67) * mm});
            skLineSegment(sketch, "E609", {"start": v(52.04, -28.67) * mm, "end": v(50.38, -26.43) * mm});
            skLineSegment(sketch, "E610", {"start": v(50.38, -26.43) * mm, "end": v(50.05, -24.76) * mm});
            skLineSegment(sketch, "E611", {"start": v(50.05, -24.76) * mm, "end": v(50.57, -22.93) * mm});
            skLineSegment(sketch, "E612", {"start": v(50.57, -22.93) * mm, "end": v(51.3, -20.4) * mm});
            skLineSegment(sketch, "E613", {"start": v(51.3, -20.4) * mm, "end": v(51.45, -18.1) * mm});
            skLineSegment(sketch, "E614", {"start": v(51.45, -18.1) * mm, "end": v(51.34, -16.56) * mm});
            skLineSegment(sketch, "E615", {"start": v(51.34, -16.56) * mm, "end": v(52.5, -18.9) * mm});
            skLineSegment(sketch, "E616", {"start": v(52.5, -18.9) * mm, "end": v(53.79, -21.95) * mm});
            skLineSegment(sketch, "E617", {"start": v(53.79, -21.95) * mm, "end": v(54.36, -23.1) * mm});
            skLineSegment(sketch, "E618", {"start": v(54.36, -23.1) * mm, "end": v(54.97, -19.79) * mm});
            skLineSegment(sketch, "E619", {"start": v(54.97, -19.79) * mm, "end": v(55.95, -15.23) * mm});
            skLineSegment(sketch, "E620", {"start": v(55.95, -15.23) * mm, "end": v(56.5, -13.2) * mm});
            skLineSegment(sketch, "E621", {"start": v(56.5, -13.2) * mm, "end": v(57.21, -10.82) * mm});
            skLineSegment(sketch, "E622", {"start": v(56.65, -18.17) * mm, "end": v(56.58, -19) * mm});
            skLineSegment(sketch, "E623", {"start": v(56.58, -19) * mm, "end": v(56.7, -20.24) * mm});
            skLineSegment(sketch, "E624", {"start": v(56.7, -20.24) * mm, "end": v(57.18, -22.12) * mm});
            skLineSegment(sketch, "E625", {"start": v(57.18, -22.12) * mm, "end": v(58.6, -24.94) * mm});
            skLineSegment(sketch, "E626", {"start": v(58.6, -24.94) * mm, "end": v(59.25, -22.57) * mm});
            skLineSegment(sketch, "E627", {"start": v(59.25, -22.57) * mm, "end": v(59.83, -21.44) * mm});
            skLineSegment(sketch, "E628", {"start": v(59.83, -21.44) * mm, "end": v(60.72, -20.54) * mm});
            skLineSegment(sketch, "E629", {"start": v(60.72, -20.54) * mm, "end": v(60.4, -21.35) * mm});
            skLineSegment(sketch, "E630", {"start": v(60.4, -21.35) * mm, "end": v(60.33, -22.43) * mm});
            skLineSegment(sketch, "E631", {"start": v(60.33, -22.43) * mm, "end": v(60.6, -23.8) * mm});
            skLineSegment(sketch, "E632", {"start": v(60.6, -23.8) * mm, "end": v(61.22, -25.4) * mm});
            skLineSegment(sketch, "E633", {"start": v(61.22, -25.4) * mm, "end": v(61.7, -26.66) * mm});
            skLineSegment(sketch, "E634", {"start": v(61.7, -26.66) * mm, "end": v(62.02, -27.3) * mm});
            skLineSegment(sketch, "E635", {"start": v(62.02, -27.3) * mm, "end": v(61.76, -27.97) * mm});
            skLineSegment(sketch, "E636", {"start": v(61.76, -27.97) * mm, "end": v(60.45, -29.78) * mm});
            skLineSegment(sketch, "E637", {"start": v(60.45, -29.78) * mm, "end": v(58.53, -30.73) * mm});
            skLineSegment(sketch, "E638", {"start": v(58.53, -30.73) * mm, "end": v(54.33, -29.34) * mm});
            skLineSegment(sketch, "E639", {"start": v(54.33, -29.34) * mm, "end": v(52.8, -28.3) * mm});
            skLineSegment(sketch, "E640", {"start": v(52.8, -28.3) * mm, "end": v(52, -27.1) * mm});
            skLineSegment(sketch, "E641", {"start": v(52, -27.1) * mm, "end": v(51.6, -25.56) * mm});
            skLineSegment(sketch, "E642", {"start": v(51.6, -25.56) * mm, "end": v(51.87, -23.82) * mm});
            skLineSegment(sketch, "E643", {"start": v(51.87, -23.82) * mm, "end": v(52.24, -21.96) * mm});
            skLineSegment(sketch, "E644", {"start": v(52.24, -21.96) * mm, "end": v(52.24, -20.59) * mm});
            skLineSegment(sketch, "E645", {"start": v(52.24, -20.59) * mm, "end": v(52.99, -22.08) * mm});
            skLineSegment(sketch, "E646", {"start": v(52.99, -22.08) * mm, "end": v(53.91, -23.36) * mm});
            skLineSegment(sketch, "E647", {"start": v(53.91, -23.36) * mm, "end": v(55.38, -25.08) * mm});
            skLineSegment(sketch, "E648", {"start": v(55.38, -25.08) * mm, "end": v(55.53, -22.55) * mm});
            skLineSegment(sketch, "E649", {"start": v(55.53, -22.55) * mm, "end": v(55.85, -20.46) * mm});
            skLineSegment(sketch, "E650", {"start": v(55.85, -20.46) * mm, "end": v(56.31, -18.8) * mm});
            skLineSegment(sketch, "E651", {"start": v(56.31, -18.8) * mm, "end": v(56.65, -18.17) * mm});
            skLineSegment(sketch, "E652", {"start": v(60.24, -24.78) * mm, "end": v(60.18, -25.8) * mm});
            skLineSegment(sketch, "E653", {"start": v(60.18, -25.8) * mm, "end": v(60.5, -27.4) * mm});
            skLineSegment(sketch, "E654", {"start": v(60.5, -27.4) * mm, "end": v(60.8, -28.56) * mm});
            skLineSegment(sketch, "E655", {"start": v(60.8, -28.56) * mm, "end": v(60.64, -29.52) * mm});
            skLineSegment(sketch, "E656", {"start": v(60.64, -29.52) * mm, "end": v(58.53, -30.57) * mm});
            skLineSegment(sketch, "E657", {"start": v(58.53, -30.57) * mm, "end": v(55.83, -29.62) * mm});
            skLineSegment(sketch, "E658", {"start": v(55.83, -29.62) * mm, "end": v(54.2, -28.74) * mm});
            skLineSegment(sketch, "E659", {"start": v(54.2, -28.74) * mm, "end": v(53.38, -28.01) * mm});
            skLineSegment(sketch, "E660", {"start": v(53.38, -28.01) * mm, "end": v(53.04, -27.32) * mm});
            skLineSegment(sketch, "E661", {"start": v(53.04, -27.32) * mm, "end": v(52.94, -25.93) * mm});
            skLineSegment(sketch, "E662", {"start": v(52.94, -25.93) * mm, "end": v(52.94, -24.59) * mm});
            skLineSegment(sketch, "E663", {"start": v(52.94, -24.59) * mm, "end": v(52.51, -23.47) * mm});
            skLineSegment(sketch, "E664", {"start": v(52.51, -23.47) * mm, "end": v(53.6, -24.72) * mm});
            skLineSegment(sketch, "E665", {"start": v(53.6, -24.72) * mm, "end": v(55.78, -26.94) * mm});
            skLineSegment(sketch, "E666", {"start": v(55.78, -26.94) * mm, "end": v(56.47, -27.45) * mm});
            skLineSegment(sketch, "E667", {"start": v(56.47, -27.45) * mm, "end": v(56.57, -25.83) * mm});
            skLineSegment(sketch, "E668", {"start": v(56.57, -25.83) * mm, "end": v(56.91, -24.57) * mm});
            skLineSegment(sketch, "E669", {"start": v(56.91, -24.57) * mm, "end": v(57.21, -26.08) * mm});
            skLineSegment(sketch, "E670", {"start": v(57.21, -26.08) * mm, "end": v(57.77, -27.2) * mm});
            skLineSegment(sketch, "E671", {"start": v(57.77, -27.2) * mm, "end": v(58.7, -28.54) * mm});
            skLineSegment(sketch, "E672", {"start": v(58.7, -28.54) * mm, "end": v(58.85, -26.65) * mm});
            skLineSegment(sketch, "E673", {"start": v(58.85, -26.65) * mm, "end": v(59.28, -25.57) * mm});
            skLineSegment(sketch, "E674", {"start": v(59.28, -25.57) * mm, "end": v(60.24, -24.78) * mm});
            skSolve(sketch);
        }
        {
            var Q0;
            Q0=qCreatedBy(makeId("Top.planeOp"),FACE);
            var sketch = newSketch(context, id + "F11", { "sketchPlane" : qUnion([Q0])});
            skSolve(sketch);
        }
        {
            var Q0;
            Q0 = qSketchRegion(id + "F11", true);
            var Q1;
            Q1=makeQuery(id+"F10.imprint","IMPRINT",FACE,{"disambiguationData":[TD([[makeQuery(id+"F10.imprint","IMPRINT",EDGE,{"derivedFrom":sQuery(id+"F10.wireOp",EDGE,"E433")}),-1.0]])]});
            var Q2;
            Q2=makeQuery(id+"F10.imprint","IMPRINT",FACE,{"disambiguationData":[TD([[makeQuery(id+"F10.imprint","IMPRINT",EDGE,{"derivedFrom":sQuery(id+"F10.wireOp",EDGE,"E554")}),-1.0]])]});
            extrude(context, id + "F12", {"entities" : qUnion([Q0, Q1, Q2]), "operationType" : NewBodyOperationType.ADD, "depth" : 1.27 * mm, "offsetDistance" : 25.4 * mm});
        }
    });
